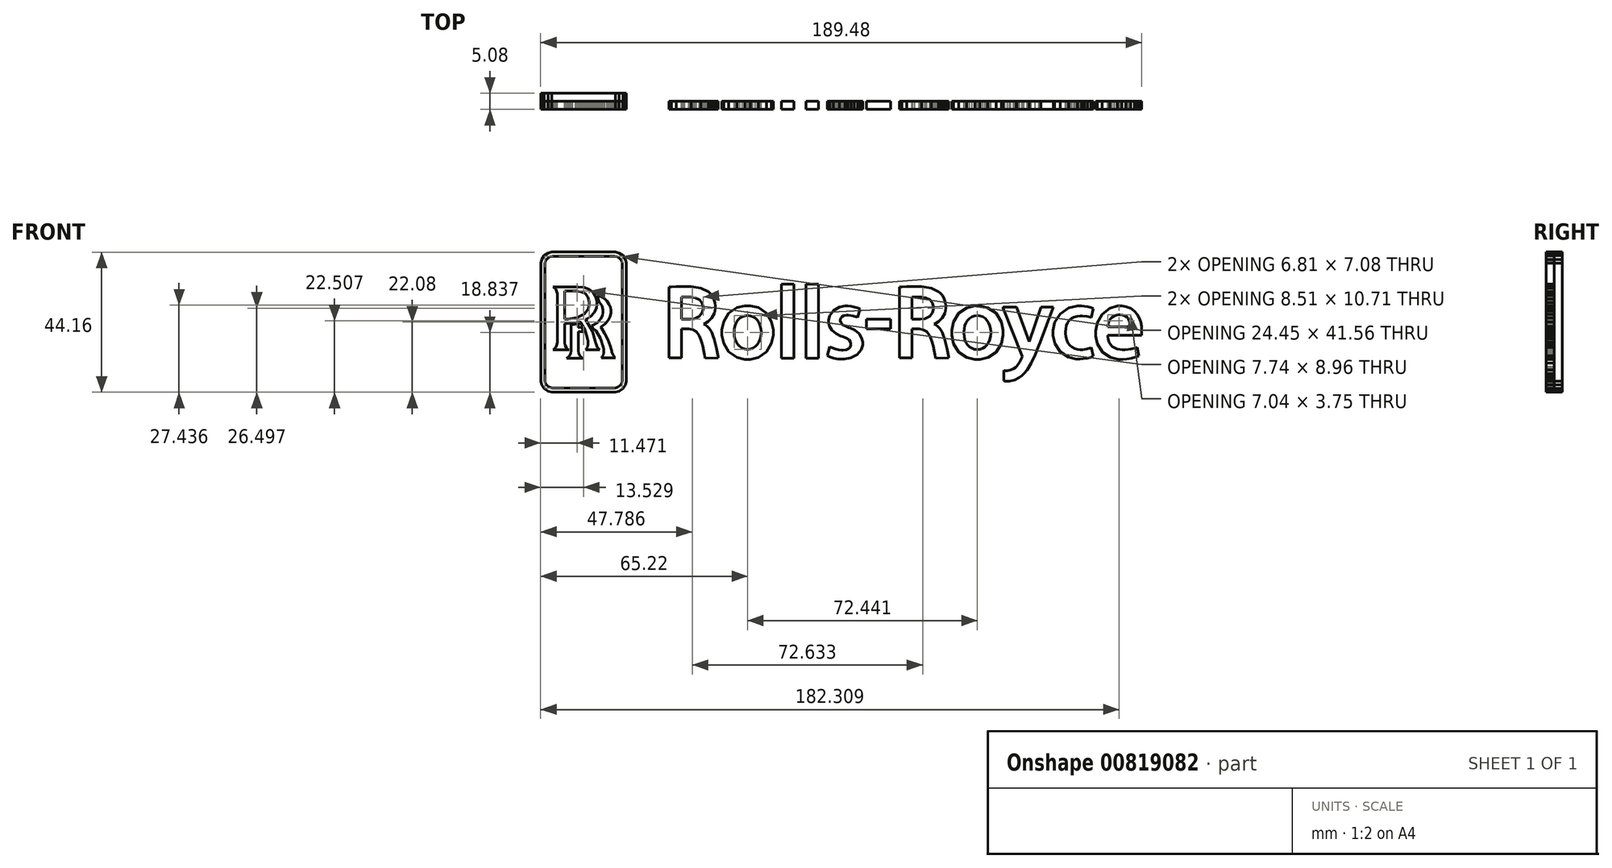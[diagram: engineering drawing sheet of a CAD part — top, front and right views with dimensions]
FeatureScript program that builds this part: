
annotation { "Feature Type Name" : "Feature", "Feature Type Description" : "" }
export const myFeature = defineFeature(function(context is Context, id is Id, definition is map)
    precondition{}
    {
        {
            var Q0;
            Q0=qCreatedBy(makeId("Front.planeOp"),FACE);
            var sketch = newSketch(context, id + "F0", { "sketchPlane" : qUnion([Q0])});
            skLineSegment(sketch, "E0", {"start": v(-93.44, 18.27) * mm, "end": v(-93.44, 18.51) * mm});
            skLineSegment(sketch, "E1", {"start": v(-93.44, 18.51) * mm, "end": v(-93.24, 19.24) * mm});
            skLineSegment(sketch, "E2", {"start": v(-93.24, 19.24) * mm, "end": v(-92.7, 20.05) * mm});
            skLineSegment(sketch, "E3", {"start": v(-92.7, 20.05) * mm, "end": v(-91.9, 20.59) * mm});
            skLineSegment(sketch, "E4", {"start": v(-91.9, 20.59) * mm, "end": v(-91.16, 20.78) * mm});
            skLineSegment(sketch, "E5", {"start": v(-91.16, 20.78) * mm, "end": v(-90.92, 20.78) * mm});
            skLineSegment(sketch, "E6", {"start": v(-90.92, 20.78) * mm, "end": v(-71.52, 20.78) * mm});
            skLineSegment(sketch, "E7", {"start": v(-71.52, 20.78) * mm, "end": v(-71.28, 20.78) * mm});
            skLineSegment(sketch, "E8", {"start": v(-71.28, 20.78) * mm, "end": v(-70.53, 20.59) * mm});
            skLineSegment(sketch, "E9", {"start": v(-70.53, 20.59) * mm, "end": v(-69.73, 20.05) * mm});
            skLineSegment(sketch, "E10", {"start": v(-69.73, 20.05) * mm, "end": v(-69.18, 19.24) * mm});
            skLineSegment(sketch, "E11", {"start": v(-69.18, 19.24) * mm, "end": v(-68.98, 18.51) * mm});
            skLineSegment(sketch, "E12", {"start": v(-68.98, 18.51) * mm, "end": v(-68.98, 18.27) * mm});
            skLineSegment(sketch, "E13", {"start": v(-68.98, 18.27) * mm, "end": v(-68.98, -18.26) * mm});
            skLineSegment(sketch, "E14", {"start": v(-68.98, -18.26) * mm, "end": v(-68.98, -18.5) * mm});
            skLineSegment(sketch, "E15", {"start": v(-68.98, -18.5) * mm, "end": v(-69.18, -19.24) * mm});
            skLineSegment(sketch, "E16", {"start": v(-69.18, -19.24) * mm, "end": v(-69.73, -20.04) * mm});
            skLineSegment(sketch, "E17", {"start": v(-69.73, -20.04) * mm, "end": v(-70.53, -20.58) * mm});
            skLineSegment(sketch, "E18", {"start": v(-70.53, -20.58) * mm, "end": v(-71.28, -20.78) * mm});
            skLineSegment(sketch, "E19", {"start": v(-71.28, -20.78) * mm, "end": v(-71.52, -20.78) * mm});
            skLineSegment(sketch, "E20", {"start": v(-71.52, -20.78) * mm, "end": v(-90.92, -20.78) * mm});
            skLineSegment(sketch, "E21", {"start": v(-90.92, -20.78) * mm, "end": v(-91.16, -20.78) * mm});
            skLineSegment(sketch, "E22", {"start": v(-91.16, -20.78) * mm, "end": v(-91.9, -20.58) * mm});
            skLineSegment(sketch, "E23", {"start": v(-91.9, -20.58) * mm, "end": v(-92.7, -20.04) * mm});
            skLineSegment(sketch, "E24", {"start": v(-92.7, -20.04) * mm, "end": v(-93.24, -19.24) * mm});
            skLineSegment(sketch, "E25", {"start": v(-93.24, -19.24) * mm, "end": v(-93.44, -18.5) * mm});
            skLineSegment(sketch, "E26", {"start": v(-93.44, -18.5) * mm, "end": v(-93.44, -18.26) * mm});
            skLineSegment(sketch, "E27", {"start": v(-93.44, -18.26) * mm, "end": v(-93.44, 18.27) * mm});
            skLineSegment(sketch, "E28", {"start": v(-18.65, -11.37) * mm, "end": v(-14.94, -11.37) * mm});
            skLineSegment(sketch, "E29", {"start": v(-14.94, -11.37) * mm, "end": v(-14.94, 12.03) * mm});
            skLineSegment(sketch, "E30", {"start": v(-14.94, 12.03) * mm, "end": v(-18.84, 12.03) * mm});
            skLineSegment(sketch, "E31", {"start": v(-18.84, 12.03) * mm, "end": v(-18.84, -11.37) * mm});
            skLineSegment(sketch, "E32", {"start": v(-18.84, -11.37) * mm, "end": v(-18.65, -11.37) * mm});
            skLineSegment(sketch, "E33", {"start": v(-10.88, -11.37) * mm, "end": v(-7.17, -11.37) * mm});
            skLineSegment(sketch, "E34", {"start": v(-7.17, -11.37) * mm, "end": v(-7.17, 12.03) * mm});
            skLineSegment(sketch, "E35", {"start": v(-7.17, 12.03) * mm, "end": v(-11.07, 12.03) * mm});
            skLineSegment(sketch, "E36", {"start": v(-11.07, 12.03) * mm, "end": v(-11.07, -11.37) * mm});
            skLineSegment(sketch, "E37", {"start": v(-11.07, -11.37) * mm, "end": v(-10.88, -11.37) * mm});
            skLineSegment(sketch, "E38", {"start": v(51.25, -18.5) * mm, "end": v(51.68, -18.57) * mm});
            skLineSegment(sketch, "E39", {"start": v(51.68, -18.57) * mm, "end": v(53, -18.56) * mm});
            skLineSegment(sketch, "E40", {"start": v(53, -18.56) * mm, "end": v(54.62, -18.2) * mm});
            skLineSegment(sketch, "E41", {"start": v(54.62, -18.2) * mm, "end": v(56.05, -17.5) * mm});
            skLineSegment(sketch, "E42", {"start": v(56.05, -17.5) * mm, "end": v(56.97, -16.84) * mm});
            skLineSegment(sketch, "E43", {"start": v(56.97, -16.84) * mm, "end": v(57.25, -16.58) * mm});
            skLineSegment(sketch, "E44", {"start": v(57.25, -16.58) * mm, "end": v(57.63, -16.22) * mm});
            skLineSegment(sketch, "E45", {"start": v(57.63, -16.22) * mm, "end": v(58.64, -15) * mm});
            skLineSegment(sketch, "E46", {"start": v(58.64, -15) * mm, "end": v(59.9, -12.96) * mm});
            skLineSegment(sketch, "E47", {"start": v(59.9, -12.96) * mm, "end": v(61.2, -10.18) * mm});
            skLineSegment(sketch, "E48", {"start": v(61.2, -10.18) * mm, "end": v(62.32, -7.37) * mm});
            skLineSegment(sketch, "E49", {"start": v(62.32, -7.37) * mm, "end": v(62.67, -6.42) * mm});
            skLineSegment(sketch, "E50", {"start": v(62.67, -6.42) * mm, "end": v(66.77, 4.5) * mm});
            skLineSegment(sketch, "E51", {"start": v(66.77, 4.5) * mm, "end": v(66.85, 4.74) * mm});
            skLineSegment(sketch, "E52", {"start": v(66.85, 4.74) * mm, "end": v(62.92, 4.74) * mm});
            skLineSegment(sketch, "E53", {"start": v(62.92, 4.74) * mm, "end": v(62.88, 4.63) * mm});
            skLineSegment(sketch, "E54", {"start": v(62.88, 4.63) * mm, "end": v(59.2, -6.21) * mm});
            skLineSegment(sketch, "E55", {"start": v(59.2, -6.21) * mm, "end": v(55.26, 4.63) * mm});
            skLineSegment(sketch, "E56", {"start": v(55.26, 4.63) * mm, "end": v(55.22, 4.74) * mm});
            skLineSegment(sketch, "E57", {"start": v(55.22, 4.74) * mm, "end": v(50.93, 4.74) * mm});
            skLineSegment(sketch, "E58", {"start": v(50.93, 4.74) * mm, "end": v(51.02, 4.5) * mm});
            skLineSegment(sketch, "E59", {"start": v(51.02, 4.5) * mm, "end": v(57.14, -10.84) * mm});
            skLineSegment(sketch, "E60", {"start": v(57.14, -10.84) * mm, "end": v(57.02, -11.18) * mm});
            skLineSegment(sketch, "E61", {"start": v(57.02, -11.18) * mm, "end": v(56.22, -12.7) * mm});
            skLineSegment(sketch, "E62", {"start": v(56.22, -12.7) * mm, "end": v(55.29, -13.93) * mm});
            skLineSegment(sketch, "E63", {"start": v(55.29, -13.93) * mm, "end": v(55.1, -14.13) * mm});
            skLineSegment(sketch, "E64", {"start": v(55.1, -14.13) * mm, "end": v(54.91, -14.3) * mm});
            skLineSegment(sketch, "E65", {"start": v(54.91, -14.3) * mm, "end": v(54.29, -14.73) * mm});
            skLineSegment(sketch, "E66", {"start": v(54.29, -14.73) * mm, "end": v(53.36, -15.13) * mm});
            skLineSegment(sketch, "E67", {"start": v(53.36, -15.13) * mm, "end": v(52.34, -15.3) * mm});
            skLineSegment(sketch, "E68", {"start": v(52.34, -15.3) * mm, "end": v(51.52, -15.28) * mm});
            skLineSegment(sketch, "E69", {"start": v(51.52, -15.28) * mm, "end": v(51.25, -15.24) * mm});
            skLineSegment(sketch, "E70", {"start": v(51.25, -15.24) * mm, "end": v(51.25, -18.5) * mm});
            skLineSegment(sketch, "E71", {"start": v(42.93, 5.14) * mm, "end": v(42.1, 5.14) * mm});
            skLineSegment(sketch, "E72", {"start": v(42.1, 5.14) * mm, "end": v(39.63, 4.52) * mm});
            skLineSegment(sketch, "E73", {"start": v(39.63, 4.52) * mm, "end": v(37.06, 2.78) * mm});
            skLineSegment(sketch, "E74", {"start": v(37.06, 2.78) * mm, "end": v(35.4, 0.11) * mm});
            skLineSegment(sketch, "E75", {"start": v(35.4, 0.11) * mm, "end": v(34.8, -2.45) * mm});
            skLineSegment(sketch, "E76", {"start": v(34.8, -2.45) * mm, "end": v(34.8, -3.3) * mm});
            skLineSegment(sketch, "E77", {"start": v(34.8, -3.3) * mm, "end": v(34.8, -4.17) * mm});
            skLineSegment(sketch, "E78", {"start": v(34.8, -4.17) * mm, "end": v(35.39, -6.76) * mm});
            skLineSegment(sketch, "E79", {"start": v(35.39, -6.76) * mm, "end": v(37.04, -9.44) * mm});
            skLineSegment(sketch, "E80", {"start": v(37.04, -9.44) * mm, "end": v(39.6, -11.16) * mm});
            skLineSegment(sketch, "E81", {"start": v(39.6, -11.16) * mm, "end": v(42.1, -11.78) * mm});
            skLineSegment(sketch, "E82", {"start": v(42.1, -11.78) * mm, "end": v(42.93, -11.78) * mm});
            skLineSegment(sketch, "E83", {"start": v(42.93, -11.78) * mm, "end": v(43.76, -11.78) * mm});
            skLineSegment(sketch, "E84", {"start": v(43.76, -11.78) * mm, "end": v(46.25, -11.16) * mm});
            skLineSegment(sketch, "E85", {"start": v(46.25, -11.16) * mm, "end": v(48.8, -9.44) * mm});
            skLineSegment(sketch, "E86", {"start": v(48.8, -9.44) * mm, "end": v(50.46, -6.76) * mm});
            skLineSegment(sketch, "E87", {"start": v(50.46, -6.76) * mm, "end": v(51.04, -4.17) * mm});
            skLineSegment(sketch, "E88", {"start": v(51.04, -4.17) * mm, "end": v(51.04, -3.3) * mm});
            skLineSegment(sketch, "E89", {"start": v(51.04, -3.3) * mm, "end": v(51.04, -2.45) * mm});
            skLineSegment(sketch, "E90", {"start": v(51.04, -2.45) * mm, "end": v(50.45, 0.11) * mm});
            skLineSegment(sketch, "E91", {"start": v(50.45, 0.11) * mm, "end": v(48.78, 2.78) * mm});
            skLineSegment(sketch, "E92", {"start": v(48.78, 2.78) * mm, "end": v(46.22, 4.52) * mm});
            skLineSegment(sketch, "E93", {"start": v(46.22, 4.52) * mm, "end": v(43.75, 5.14) * mm});
            skLineSegment(sketch, "E94", {"start": v(43.75, 5.14) * mm, "end": v(42.93, 5.14) * mm});
            skLineSegment(sketch, "E95", {"start": v(42.9, -8.64) * mm, "end": v(42.69, -8.64) * mm});
            skLineSegment(sketch, "E96", {"start": v(42.69, -8.64) * mm, "end": v(42.03, -8.54) * mm});
            skLineSegment(sketch, "E97", {"start": v(42.03, -8.54) * mm, "end": v(41.22, -8.26) * mm});
            skLineSegment(sketch, "E98", {"start": v(41.22, -8.26) * mm, "end": v(40.5, -7.8) * mm});
            skLineSegment(sketch, "E99", {"start": v(40.5, -7.8) * mm, "end": v(39.87, -7.18) * mm});
            skLineSegment(sketch, "E100", {"start": v(39.87, -7.18) * mm, "end": v(39.36, -6.4) * mm});
            skLineSegment(sketch, "E101", {"start": v(39.36, -6.4) * mm, "end": v(38.98, -5.5) * mm});
            skLineSegment(sketch, "E102", {"start": v(38.98, -5.5) * mm, "end": v(38.75, -4.45) * mm});
            skLineSegment(sketch, "E103", {"start": v(38.75, -4.45) * mm, "end": v(38.66, -3.58) * mm});
            skLineSegment(sketch, "E104", {"start": v(38.66, -3.58) * mm, "end": v(38.66, -3.29) * mm});
            skLineSegment(sketch, "E105", {"start": v(38.66, -3.29) * mm, "end": v(38.66, -3) * mm});
            skLineSegment(sketch, "E106", {"start": v(38.66, -3) * mm, "end": v(38.75, -2.12) * mm});
            skLineSegment(sketch, "E107", {"start": v(38.75, -2.12) * mm, "end": v(38.98, -1.08) * mm});
            skLineSegment(sketch, "E108", {"start": v(38.98, -1.08) * mm, "end": v(39.36, -0.17) * mm});
            skLineSegment(sketch, "E109", {"start": v(39.36, -0.17) * mm, "end": v(39.87, 0.6) * mm});
            skLineSegment(sketch, "E110", {"start": v(39.87, 0.6) * mm, "end": v(40.5, 1.23) * mm});
            skLineSegment(sketch, "E111", {"start": v(40.5, 1.23) * mm, "end": v(41.22, 1.7) * mm});
            skLineSegment(sketch, "E112", {"start": v(41.22, 1.7) * mm, "end": v(42.03, 1.97) * mm});
            skLineSegment(sketch, "E113", {"start": v(42.03, 1.97) * mm, "end": v(42.69, 2.07) * mm});
            skLineSegment(sketch, "E114", {"start": v(42.69, 2.07) * mm, "end": v(42.9, 2.07) * mm});
            skLineSegment(sketch, "E115", {"start": v(42.9, 2.07) * mm, "end": v(43.13, 2.07) * mm});
            skLineSegment(sketch, "E116", {"start": v(43.13, 2.07) * mm, "end": v(43.8, 1.97) * mm});
            skLineSegment(sketch, "E117", {"start": v(43.8, 1.97) * mm, "end": v(44.62, 1.7) * mm});
            skLineSegment(sketch, "E118", {"start": v(44.62, 1.7) * mm, "end": v(45.35, 1.23) * mm});
            skLineSegment(sketch, "E119", {"start": v(45.35, 1.23) * mm, "end": v(45.97, 0.6) * mm});
            skLineSegment(sketch, "E120", {"start": v(45.97, 0.6) * mm, "end": v(46.48, -0.17) * mm});
            skLineSegment(sketch, "E121", {"start": v(46.48, -0.17) * mm, "end": v(46.86, -1.08) * mm});
            skLineSegment(sketch, "E122", {"start": v(46.86, -1.08) * mm, "end": v(47.1, -2.12) * mm});
            skLineSegment(sketch, "E123", {"start": v(47.1, -2.12) * mm, "end": v(47.18, -3) * mm});
            skLineSegment(sketch, "E124", {"start": v(47.18, -3) * mm, "end": v(47.18, -3.29) * mm});
            skLineSegment(sketch, "E125", {"start": v(47.18, -3.29) * mm, "end": v(47.18, -3.58) * mm});
            skLineSegment(sketch, "E126", {"start": v(47.18, -3.58) * mm, "end": v(47.1, -4.45) * mm});
            skLineSegment(sketch, "E127", {"start": v(47.1, -4.45) * mm, "end": v(46.86, -5.5) * mm});
            skLineSegment(sketch, "E128", {"start": v(46.86, -5.5) * mm, "end": v(46.47, -6.4) * mm});
            skLineSegment(sketch, "E129", {"start": v(46.47, -6.4) * mm, "end": v(45.96, -7.18) * mm});
            skLineSegment(sketch, "E130", {"start": v(45.96, -7.18) * mm, "end": v(45.34, -7.8) * mm});
            skLineSegment(sketch, "E131", {"start": v(45.34, -7.8) * mm, "end": v(44.61, -8.26) * mm});
            skLineSegment(sketch, "E132", {"start": v(44.61, -8.26) * mm, "end": v(43.8, -8.54) * mm});
            skLineSegment(sketch, "E133", {"start": v(43.8, -8.54) * mm, "end": v(43.13, -8.64) * mm});
            skLineSegment(sketch, "E134", {"start": v(43.13, -8.64) * mm, "end": v(42.9, -8.64) * mm});
            skLineSegment(sketch, "E135", {"start": v(-29.51, 5.18) * mm, "end": v(-30.35, 5.18) * mm});
            skLineSegment(sketch, "E136", {"start": v(-30.35, 5.18) * mm, "end": v(-32.87, 4.57) * mm});
            skLineSegment(sketch, "E137", {"start": v(-32.87, 4.57) * mm, "end": v(-35.43, 2.85) * mm});
            skLineSegment(sketch, "E138", {"start": v(-35.43, 2.85) * mm, "end": v(-37.07, 0.18) * mm});
            skLineSegment(sketch, "E139", {"start": v(-37.07, 0.18) * mm, "end": v(-37.64, -2.4) * mm});
            skLineSegment(sketch, "E140", {"start": v(-37.64, -2.4) * mm, "end": v(-37.64, -3.26) * mm});
            skLineSegment(sketch, "E141", {"start": v(-37.64, -3.26) * mm, "end": v(-37.64, -4.13) * mm});
            skLineSegment(sketch, "E142", {"start": v(-37.64, -4.13) * mm, "end": v(-37.07, -6.72) * mm});
            skLineSegment(sketch, "E143", {"start": v(-37.07, -6.72) * mm, "end": v(-35.43, -9.4) * mm});
            skLineSegment(sketch, "E144", {"start": v(-35.43, -9.4) * mm, "end": v(-32.87, -11.12) * mm});
            skLineSegment(sketch, "E145", {"start": v(-32.87, -11.12) * mm, "end": v(-30.35, -11.74) * mm});
            skLineSegment(sketch, "E146", {"start": v(-30.35, -11.74) * mm, "end": v(-29.51, -11.74) * mm});
            skLineSegment(sketch, "E147", {"start": v(-29.51, -11.74) * mm, "end": v(-28.67, -11.74) * mm});
            skLineSegment(sketch, "E148", {"start": v(-28.67, -11.74) * mm, "end": v(-26.15, -11.12) * mm});
            skLineSegment(sketch, "E149", {"start": v(-26.15, -11.12) * mm, "end": v(-23.6, -9.4) * mm});
            skLineSegment(sketch, "E150", {"start": v(-23.6, -9.4) * mm, "end": v(-21.97, -6.72) * mm});
            skLineSegment(sketch, "E151", {"start": v(-21.97, -6.72) * mm, "end": v(-21.4, -4.13) * mm});
            skLineSegment(sketch, "E152", {"start": v(-21.4, -4.13) * mm, "end": v(-21.4, -3.26) * mm});
            skLineSegment(sketch, "E153", {"start": v(-21.4, -3.26) * mm, "end": v(-21.4, -2.4) * mm});
            skLineSegment(sketch, "E154", {"start": v(-21.4, -2.4) * mm, "end": v(-21.97, 0.18) * mm});
            skLineSegment(sketch, "E155", {"start": v(-21.97, 0.18) * mm, "end": v(-23.6, 2.85) * mm});
            skLineSegment(sketch, "E156", {"start": v(-23.6, 2.85) * mm, "end": v(-26.15, 4.57) * mm});
            skLineSegment(sketch, "E157", {"start": v(-26.15, 4.57) * mm, "end": v(-28.67, 5.18) * mm});
            skLineSegment(sketch, "E158", {"start": v(-28.67, 5.18) * mm, "end": v(-29.51, 5.18) * mm});
            skLineSegment(sketch, "E159", {"start": v(-29.53, -8.6) * mm, "end": v(-29.75, -8.6) * mm});
            skLineSegment(sketch, "E160", {"start": v(-29.75, -8.6) * mm, "end": v(-30.41, -8.5) * mm});
            skLineSegment(sketch, "E161", {"start": v(-30.41, -8.5) * mm, "end": v(-31.22, -8.21) * mm});
            skLineSegment(sketch, "E162", {"start": v(-31.22, -8.21) * mm, "end": v(-31.94, -7.75) * mm});
            skLineSegment(sketch, "E163", {"start": v(-31.94, -7.75) * mm, "end": v(-32.57, -7.13) * mm});
            skLineSegment(sketch, "E164", {"start": v(-32.57, -7.13) * mm, "end": v(-33.07, -6.35) * mm});
            skLineSegment(sketch, "E165", {"start": v(-33.07, -6.35) * mm, "end": v(-33.46, -5.44) * mm});
            skLineSegment(sketch, "E166", {"start": v(-33.46, -5.44) * mm, "end": v(-33.7, -4.4) * mm});
            skLineSegment(sketch, "E167", {"start": v(-33.7, -4.4) * mm, "end": v(-33.78, -3.53) * mm});
            skLineSegment(sketch, "E168", {"start": v(-33.78, -3.53) * mm, "end": v(-33.78, -3.24) * mm});
            skLineSegment(sketch, "E169", {"start": v(-33.78, -3.24) * mm, "end": v(-33.78, -2.95) * mm});
            skLineSegment(sketch, "E170", {"start": v(-33.78, -2.95) * mm, "end": v(-33.7, -2.08) * mm});
            skLineSegment(sketch, "E171", {"start": v(-33.7, -2.08) * mm, "end": v(-33.46, -1.04) * mm});
            skLineSegment(sketch, "E172", {"start": v(-33.46, -1.04) * mm, "end": v(-33.07, -0.12) * mm});
            skLineSegment(sketch, "E173", {"start": v(-33.07, -0.12) * mm, "end": v(-32.57, 0.65) * mm});
            skLineSegment(sketch, "E174", {"start": v(-32.57, 0.65) * mm, "end": v(-31.94, 1.27) * mm});
            skLineSegment(sketch, "E175", {"start": v(-31.94, 1.27) * mm, "end": v(-31.22, 1.73) * mm});
            skLineSegment(sketch, "E176", {"start": v(-31.22, 1.73) * mm, "end": v(-30.41, 2.02) * mm});
            skLineSegment(sketch, "E177", {"start": v(-30.41, 2.02) * mm, "end": v(-29.75, 2.11) * mm});
            skLineSegment(sketch, "E178", {"start": v(-29.75, 2.11) * mm, "end": v(-29.53, 2.11) * mm});
            skLineSegment(sketch, "E179", {"start": v(-29.53, 2.11) * mm, "end": v(-29.3, 2.11) * mm});
            skLineSegment(sketch, "E180", {"start": v(-29.3, 2.11) * mm, "end": v(-28.64, 2.02) * mm});
            skLineSegment(sketch, "E181", {"start": v(-28.64, 2.02) * mm, "end": v(-27.82, 1.73) * mm});
            skLineSegment(sketch, "E182", {"start": v(-27.82, 1.73) * mm, "end": v(-27.1, 1.27) * mm});
            skLineSegment(sketch, "E183", {"start": v(-27.1, 1.27) * mm, "end": v(-26.47, 0.65) * mm});
            skLineSegment(sketch, "E184", {"start": v(-26.47, 0.65) * mm, "end": v(-25.96, -0.12) * mm});
            skLineSegment(sketch, "E185", {"start": v(-25.96, -0.12) * mm, "end": v(-25.58, -1.04) * mm});
            skLineSegment(sketch, "E186", {"start": v(-25.58, -1.04) * mm, "end": v(-25.35, -2.08) * mm});
            skLineSegment(sketch, "E187", {"start": v(-25.35, -2.08) * mm, "end": v(-25.26, -2.95) * mm});
            skLineSegment(sketch, "E188", {"start": v(-25.26, -2.95) * mm, "end": v(-25.26, -3.24) * mm});
            skLineSegment(sketch, "E189", {"start": v(-25.26, -3.24) * mm, "end": v(-25.26, -3.53) * mm});
            skLineSegment(sketch, "E190", {"start": v(-25.26, -3.53) * mm, "end": v(-25.35, -4.4) * mm});
            skLineSegment(sketch, "E191", {"start": v(-25.35, -4.4) * mm, "end": v(-25.59, -5.44) * mm});
            skLineSegment(sketch, "E192", {"start": v(-25.59, -5.44) * mm, "end": v(-25.97, -6.35) * mm});
            skLineSegment(sketch, "E193", {"start": v(-25.97, -6.35) * mm, "end": v(-26.48, -7.13) * mm});
            skLineSegment(sketch, "E194", {"start": v(-26.48, -7.13) * mm, "end": v(-27.1, -7.75) * mm});
            skLineSegment(sketch, "E195", {"start": v(-27.1, -7.75) * mm, "end": v(-27.83, -8.21) * mm});
            skLineSegment(sketch, "E196", {"start": v(-27.83, -8.21) * mm, "end": v(-28.64, -8.5) * mm});
            skLineSegment(sketch, "E197", {"start": v(-28.64, -8.5) * mm, "end": v(-29.3, -8.6) * mm});
            skLineSegment(sketch, "E198", {"start": v(-29.3, -8.6) * mm, "end": v(-29.53, -8.6) * mm});
            skLineSegment(sketch, "E199", {"start": v(7.92, -2.07) * mm, "end": v(15.58, -2.07) * mm});
            skLineSegment(sketch, "E200", {"start": v(15.58, -2.07) * mm, "end": v(15.58, 0.87) * mm});
            skLineSegment(sketch, "E201", {"start": v(15.58, 0.87) * mm, "end": v(7.92, 0.87) * mm});
            skLineSegment(sketch, "E202", {"start": v(7.92, 0.87) * mm, "end": v(7.92, -2.07) * mm});
            skLineSegment(sketch, "E203", {"start": v(-40.29, -4.65) * mm, "end": v(-40.08, -5.3) * mm});
            skLineSegment(sketch, "E204", {"start": v(-40.08, -5.3) * mm, "end": v(-39.33, -8.36) * mm});
            skLineSegment(sketch, "E205", {"start": v(-39.33, -8.36) * mm, "end": v(-38.82, -10.92) * mm});
            skLineSegment(sketch, "E206", {"start": v(-38.82, -10.92) * mm, "end": v(-38.75, -11.3) * mm});
            skLineSegment(sketch, "E207", {"start": v(-38.75, -11.3) * mm, "end": v(-42.91, -11.33) * mm});
            skLineSegment(sketch, "E208", {"start": v(-42.91, -11.33) * mm, "end": v(-42.96, -11.06) * mm});
            skLineSegment(sketch, "E209", {"start": v(-42.96, -11.06) * mm, "end": v(-43.1, -10.24) * mm});
            skLineSegment(sketch, "E210", {"start": v(-43.1, -10.24) * mm, "end": v(-43.32, -8.98) * mm});
            skLineSegment(sketch, "E211", {"start": v(-43.32, -8.98) * mm, "end": v(-43.65, -7.54) * mm});
            skLineSegment(sketch, "E212", {"start": v(-43.65, -7.54) * mm, "end": v(-43.98, -6.34) * mm});
            skLineSegment(sketch, "E213", {"start": v(-43.98, -6.34) * mm, "end": v(-44.1, -5.95) * mm});
            skLineSegment(sketch, "E214", {"start": v(-44.1, -5.95) * mm, "end": v(-44.24, -5.51) * mm});
            skLineSegment(sketch, "E215", {"start": v(-44.24, -5.51) * mm, "end": v(-44.79, -4.23) * mm});
            skLineSegment(sketch, "E216", {"start": v(-44.79, -4.23) * mm, "end": v(-45.67, -3.03) * mm});
            skLineSegment(sketch, "E217", {"start": v(-45.67, -3.03) * mm, "end": v(-46.85, -2.32) * mm});
            skLineSegment(sketch, "E218", {"start": v(-46.85, -2.32) * mm, "end": v(-48.06, -2.1) * mm});
            skLineSegment(sketch, "E219", {"start": v(-48.06, -2.1) * mm, "end": v(-48.46, -2.1) * mm});
            skLineSegment(sketch, "E220", {"start": v(-48.46, -2.1) * mm, "end": v(-50.36, -2.1) * mm});
            skLineSegment(sketch, "E221", {"start": v(-50.36, -2.1) * mm, "end": v(-50.36, -11.3) * mm});
            skLineSegment(sketch, "E222", {"start": v(-50.36, -11.3) * mm, "end": v(-54.28, -11.3) * mm});
            skLineSegment(sketch, "E223", {"start": v(-54.28, -11.3) * mm, "end": v(-54.28, 11.12) * mm});
            skLineSegment(sketch, "E224", {"start": v(-54.28, 11.12) * mm, "end": v(-53.57, 11.12) * mm});
            skLineSegment(sketch, "E225", {"start": v(-53.57, 11.12) * mm, "end": v(-51.96, 11.18) * mm});
            skLineSegment(sketch, "E226", {"start": v(-51.96, 11.18) * mm, "end": v(-51.42, 11.18) * mm});
            skLineSegment(sketch, "E227", {"start": v(-51.42, 11.18) * mm, "end": v(-48.27, 11.18) * mm});
            skLineSegment(sketch, "E228", {"start": v(-48.27, 11.18) * mm, "end": v(-47.26, 11.18) * mm});
            skLineSegment(sketch, "E229", {"start": v(-47.26, 11.18) * mm, "end": v(-44.26, 10.7) * mm});
            skLineSegment(sketch, "E230", {"start": v(-44.26, 10.7) * mm, "end": v(-41.9, 9.58) * mm});
            skLineSegment(sketch, "E231", {"start": v(-41.9, 9.58) * mm, "end": v(-41.54, 9.26) * mm});
            skLineSegment(sketch, "E232", {"start": v(-41.54, 9.26) * mm, "end": v(-41.32, 9.07) * mm});
            skLineSegment(sketch, "E233", {"start": v(-41.32, 9.07) * mm, "end": v(-40.74, 8.38) * mm});
            skLineSegment(sketch, "E234", {"start": v(-40.74, 8.38) * mm, "end": v(-40.15, 7.33) * mm});
            skLineSegment(sketch, "E235", {"start": v(-40.15, 7.33) * mm, "end": v(-39.79, 6.13) * mm});
            skLineSegment(sketch, "E236", {"start": v(-39.79, 6.13) * mm, "end": v(-39.67, 5.15) * mm});
            skLineSegment(sketch, "E237", {"start": v(-39.67, 5.15) * mm, "end": v(-39.67, 4.82) * mm});
            skLineSegment(sketch, "E238", {"start": v(-39.67, 4.82) * mm, "end": v(-39.67, 4.33) * mm});
            skLineSegment(sketch, "E239", {"start": v(-39.67, 4.33) * mm, "end": v(-39.97, 2.83) * mm});
            skLineSegment(sketch, "E240", {"start": v(-39.97, 2.83) * mm, "end": v(-40.77, 1.28) * mm});
            skLineSegment(sketch, "E241", {"start": v(-40.77, 1.28) * mm, "end": v(-41.94, 0.15) * mm});
            skLineSegment(sketch, "E242", {"start": v(-41.94, 0.15) * mm, "end": v(-42.95, -0.46) * mm});
            skLineSegment(sketch, "E243", {"start": v(-42.95, -0.46) * mm, "end": v(-43.32, -0.6) * mm});
            skLineSegment(sketch, "E244", {"start": v(-43.32, -0.6) * mm, "end": v(-43.06, -0.72) * mm});
            skLineSegment(sketch, "E245", {"start": v(-43.06, -0.72) * mm, "end": v(-42.35, -1.2) * mm});
            skLineSegment(sketch, "E246", {"start": v(-42.35, -1.2) * mm, "end": v(-41.54, -2.03) * mm});
            skLineSegment(sketch, "E247", {"start": v(-41.54, -2.03) * mm, "end": v(-40.87, -3.17) * mm});
            skLineSegment(sketch, "E248", {"start": v(-40.87, -3.17) * mm, "end": v(-40.4, -4.27) * mm});
            skLineSegment(sketch, "E249", {"start": v(-40.4, -4.27) * mm, "end": v(-40.29, -4.65) * mm});
            skLineSegment(sketch, "E250", {"start": v(-47.86, 7.96) * mm, "end": v(-49.16, 7.96) * mm});
            skLineSegment(sketch, "E251", {"start": v(-49.16, 7.96) * mm, "end": v(-49.34, 7.96) * mm});
            skLineSegment(sketch, "E252", {"start": v(-49.34, 7.96) * mm, "end": v(-49.86, 7.94) * mm});
            skLineSegment(sketch, "E253", {"start": v(-49.86, 7.94) * mm, "end": v(-50.23, 7.92) * mm});
            skLineSegment(sketch, "E254", {"start": v(-50.23, 7.92) * mm, "end": v(-50.36, 7.92) * mm});
            skLineSegment(sketch, "E255", {"start": v(-50.36, 7.92) * mm, "end": v(-50.36, 0.88) * mm});
            skLineSegment(sketch, "E256", {"start": v(-50.36, 0.88) * mm, "end": v(-48.08, 0.88) * mm});
            skLineSegment(sketch, "E257", {"start": v(-48.08, 0.88) * mm, "end": v(-47.61, 0.88) * mm});
            skLineSegment(sketch, "E258", {"start": v(-47.61, 0.88) * mm, "end": v(-46.23, 1.13) * mm});
            skLineSegment(sketch, "E259", {"start": v(-46.23, 1.13) * mm, "end": v(-44.8, 1.84) * mm});
            skLineSegment(sketch, "E260", {"start": v(-44.8, 1.84) * mm, "end": v(-43.88, 2.97) * mm});
            skLineSegment(sketch, "E261", {"start": v(-43.88, 2.97) * mm, "end": v(-43.55, 4.09) * mm});
            skLineSegment(sketch, "E262", {"start": v(-43.55, 4.09) * mm, "end": v(-43.55, 4.46) * mm});
            skLineSegment(sketch, "E263", {"start": v(-43.55, 4.46) * mm, "end": v(-43.55, 4.84) * mm});
            skLineSegment(sketch, "E264", {"start": v(-43.55, 4.84) * mm, "end": v(-43.83, 5.97) * mm});
            skLineSegment(sketch, "E265", {"start": v(-43.83, 5.97) * mm, "end": v(-44.65, 7.06) * mm});
            skLineSegment(sketch, "E266", {"start": v(-44.65, 7.06) * mm, "end": v(-46, 7.73) * mm});
            skLineSegment(sketch, "E267", {"start": v(-46, 7.73) * mm, "end": v(-47.4, 7.96) * mm});
            skLineSegment(sketch, "E268", {"start": v(-47.4, 7.96) * mm, "end": v(-47.86, 7.96) * mm});
            skLineSegment(sketch, "E269", {"start": v(32.35, -4.65) * mm, "end": v(32.55, -5.3) * mm});
            skLineSegment(sketch, "E270", {"start": v(32.55, -5.3) * mm, "end": v(33.3, -8.36) * mm});
            skLineSegment(sketch, "E271", {"start": v(33.3, -8.36) * mm, "end": v(33.8, -10.92) * mm});
            skLineSegment(sketch, "E272", {"start": v(33.8, -10.92) * mm, "end": v(33.88, -11.3) * mm});
            skLineSegment(sketch, "E273", {"start": v(33.88, -11.3) * mm, "end": v(29.72, -11.33) * mm});
            skLineSegment(sketch, "E274", {"start": v(29.72, -11.33) * mm, "end": v(29.68, -11.06) * mm});
            skLineSegment(sketch, "E275", {"start": v(29.68, -11.06) * mm, "end": v(29.54, -10.24) * mm});
            skLineSegment(sketch, "E276", {"start": v(29.54, -10.24) * mm, "end": v(29.3, -8.98) * mm});
            skLineSegment(sketch, "E277", {"start": v(29.3, -8.98) * mm, "end": v(28.99, -7.54) * mm});
            skLineSegment(sketch, "E278", {"start": v(28.99, -7.54) * mm, "end": v(28.66, -6.34) * mm});
            skLineSegment(sketch, "E279", {"start": v(28.66, -6.34) * mm, "end": v(28.53, -5.95) * mm});
            skLineSegment(sketch, "E280", {"start": v(28.53, -5.95) * mm, "end": v(28.39, -5.51) * mm});
            skLineSegment(sketch, "E281", {"start": v(28.39, -5.51) * mm, "end": v(27.85, -4.23) * mm});
            skLineSegment(sketch, "E282", {"start": v(27.85, -4.23) * mm, "end": v(26.97, -3.03) * mm});
            skLineSegment(sketch, "E283", {"start": v(26.97, -3.03) * mm, "end": v(25.78, -2.32) * mm});
            skLineSegment(sketch, "E284", {"start": v(25.78, -2.32) * mm, "end": v(24.58, -2.1) * mm});
            skLineSegment(sketch, "E285", {"start": v(24.58, -2.1) * mm, "end": v(24.18, -2.1) * mm});
            skLineSegment(sketch, "E286", {"start": v(24.18, -2.1) * mm, "end": v(22.28, -2.1) * mm});
            skLineSegment(sketch, "E287", {"start": v(22.28, -2.1) * mm, "end": v(22.28, -11.3) * mm});
            skLineSegment(sketch, "E288", {"start": v(22.28, -11.3) * mm, "end": v(18.35, -11.3) * mm});
            skLineSegment(sketch, "E289", {"start": v(18.35, -11.3) * mm, "end": v(18.35, 11.12) * mm});
            skLineSegment(sketch, "E290", {"start": v(18.35, 11.12) * mm, "end": v(19.06, 11.12) * mm});
            skLineSegment(sketch, "E291", {"start": v(19.06, 11.12) * mm, "end": v(20.67, 11.18) * mm});
            skLineSegment(sketch, "E292", {"start": v(20.67, 11.18) * mm, "end": v(21.2, 11.18) * mm});
            skLineSegment(sketch, "E293", {"start": v(21.2, 11.18) * mm, "end": v(24.37, 11.18) * mm});
            skLineSegment(sketch, "E294", {"start": v(24.37, 11.18) * mm, "end": v(25.37, 11.18) * mm});
            skLineSegment(sketch, "E295", {"start": v(25.37, 11.18) * mm, "end": v(28.38, 10.7) * mm});
            skLineSegment(sketch, "E296", {"start": v(28.38, 10.7) * mm, "end": v(30.73, 9.58) * mm});
            skLineSegment(sketch, "E297", {"start": v(30.73, 9.58) * mm, "end": v(31.09, 9.26) * mm});
            skLineSegment(sketch, "E298", {"start": v(31.09, 9.26) * mm, "end": v(31.31, 9.07) * mm});
            skLineSegment(sketch, "E299", {"start": v(31.31, 9.07) * mm, "end": v(31.9, 8.38) * mm});
            skLineSegment(sketch, "E300", {"start": v(31.9, 8.38) * mm, "end": v(32.48, 7.33) * mm});
            skLineSegment(sketch, "E301", {"start": v(32.48, 7.33) * mm, "end": v(32.84, 6.13) * mm});
            skLineSegment(sketch, "E302", {"start": v(32.84, 6.13) * mm, "end": v(32.97, 5.15) * mm});
            skLineSegment(sketch, "E303", {"start": v(32.97, 5.15) * mm, "end": v(32.97, 4.82) * mm});
            skLineSegment(sketch, "E304", {"start": v(32.97, 4.82) * mm, "end": v(32.97, 4.33) * mm});
            skLineSegment(sketch, "E305", {"start": v(32.97, 4.33) * mm, "end": v(32.67, 2.83) * mm});
            skLineSegment(sketch, "E306", {"start": v(32.67, 2.83) * mm, "end": v(31.86, 1.28) * mm});
            skLineSegment(sketch, "E307", {"start": v(31.86, 1.28) * mm, "end": v(30.7, 0.15) * mm});
            skLineSegment(sketch, "E308", {"start": v(30.7, 0.15) * mm, "end": v(29.68, -0.46) * mm});
            skLineSegment(sketch, "E309", {"start": v(29.68, -0.46) * mm, "end": v(29.32, -0.6) * mm});
            skLineSegment(sketch, "E310", {"start": v(29.32, -0.6) * mm, "end": v(29.57, -0.72) * mm});
            skLineSegment(sketch, "E311", {"start": v(29.57, -0.72) * mm, "end": v(30.28, -1.2) * mm});
            skLineSegment(sketch, "E312", {"start": v(30.28, -1.2) * mm, "end": v(31.09, -2.03) * mm});
            skLineSegment(sketch, "E313", {"start": v(31.09, -2.03) * mm, "end": v(31.76, -3.17) * mm});
            skLineSegment(sketch, "E314", {"start": v(31.76, -3.17) * mm, "end": v(32.22, -4.27) * mm});
            skLineSegment(sketch, "E315", {"start": v(32.22, -4.27) * mm, "end": v(32.35, -4.65) * mm});
            skLineSegment(sketch, "E316", {"start": v(24.77, 7.96) * mm, "end": v(23.47, 7.96) * mm});
            skLineSegment(sketch, "E317", {"start": v(23.47, 7.96) * mm, "end": v(23.17, 7.96) * mm});
            skLineSegment(sketch, "E318", {"start": v(23.17, 7.96) * mm, "end": v(22.5, 7.92) * mm});
            skLineSegment(sketch, "E319", {"start": v(22.5, 7.92) * mm, "end": v(22.28, 7.92) * mm});
            skLineSegment(sketch, "E320", {"start": v(22.28, 7.92) * mm, "end": v(22.28, 0.88) * mm});
            skLineSegment(sketch, "E321", {"start": v(22.28, 0.88) * mm, "end": v(24.56, 0.88) * mm});
            skLineSegment(sketch, "E322", {"start": v(24.56, 0.88) * mm, "end": v(25.02, 0.88) * mm});
            skLineSegment(sketch, "E323", {"start": v(25.02, 0.88) * mm, "end": v(26.4, 1.13) * mm});
            skLineSegment(sketch, "E324", {"start": v(26.4, 1.13) * mm, "end": v(27.83, 1.84) * mm});
            skLineSegment(sketch, "E325", {"start": v(27.83, 1.84) * mm, "end": v(28.75, 2.97) * mm});
            skLineSegment(sketch, "E326", {"start": v(28.75, 2.97) * mm, "end": v(29.08, 4.09) * mm});
            skLineSegment(sketch, "E327", {"start": v(29.08, 4.09) * mm, "end": v(29.08, 4.46) * mm});
            skLineSegment(sketch, "E328", {"start": v(29.08, 4.46) * mm, "end": v(29.08, 4.84) * mm});
            skLineSegment(sketch, "E329", {"start": v(29.08, 4.84) * mm, "end": v(28.8, 5.97) * mm});
            skLineSegment(sketch, "E330", {"start": v(28.8, 5.97) * mm, "end": v(27.98, 7.06) * mm});
            skLineSegment(sketch, "E331", {"start": v(27.98, 7.06) * mm, "end": v(26.63, 7.73) * mm});
            skLineSegment(sketch, "E332", {"start": v(26.63, 7.73) * mm, "end": v(25.24, 7.96) * mm});
            skLineSegment(sketch, "E333", {"start": v(25.24, 7.96) * mm, "end": v(24.77, 7.96) * mm});
            skLineSegment(sketch, "E334", {"start": v(-3.67, -7.7) * mm, "end": v(-3.48, -7.82) * mm});
            skLineSegment(sketch, "E335", {"start": v(-3.48, -7.82) * mm, "end": v(-2.87, -8.1) * mm});
            skLineSegment(sketch, "E336", {"start": v(-2.87, -8.1) * mm, "end": v(-1.89, -8.46) * mm});
            skLineSegment(sketch, "E337", {"start": v(-1.89, -8.46) * mm, "end": v(-0.8, -8.7) * mm});
            skLineSegment(sketch, "E338", {"start": v(-0.8, -8.7) * mm, "end": v(0.02, -8.8) * mm});
            skLineSegment(sketch, "E339", {"start": v(0.02, -8.8) * mm, "end": v(0.3, -8.8) * mm});
            skLineSegment(sketch, "E340", {"start": v(0.3, -8.8) * mm, "end": v(0.6, -8.8) * mm});
            skLineSegment(sketch, "E341", {"start": v(0.6, -8.8) * mm, "end": v(1.53, -8.68) * mm});
            skLineSegment(sketch, "E342", {"start": v(1.53, -8.68) * mm, "end": v(2.36, -8.33) * mm});
            skLineSegment(sketch, "E343", {"start": v(2.36, -8.33) * mm, "end": v(2.84, -7.77) * mm});
            skLineSegment(sketch, "E344", {"start": v(2.84, -7.77) * mm, "end": v(2.99, -7.2) * mm});
            skLineSegment(sketch, "E345", {"start": v(2.99, -7.2) * mm, "end": v(2.99, -7) * mm});
            skLineSegment(sketch, "E346", {"start": v(2.99, -7) * mm, "end": v(2.99, -6.8) * mm});
            skLineSegment(sketch, "E347", {"start": v(2.99, -6.8) * mm, "end": v(2.86, -6.21) * mm});
            skLineSegment(sketch, "E348", {"start": v(2.86, -6.21) * mm, "end": v(2.42, -5.6) * mm});
            skLineSegment(sketch, "E349", {"start": v(2.42, -5.6) * mm, "end": v(1.6, -5.07) * mm});
            skLineSegment(sketch, "E350", {"start": v(1.6, -5.07) * mm, "end": v(0.64, -4.66) * mm});
            skLineSegment(sketch, "E351", {"start": v(0.64, -4.66) * mm, "end": v(0.32, -4.54) * mm});
            skLineSegment(sketch, "E352", {"start": v(0.32, -4.54) * mm, "end": v(-0.19, -4.37) * mm});
            skLineSegment(sketch, "E353", {"start": v(-0.19, -4.37) * mm, "end": v(-1.63, -3.62) * mm});
            skLineSegment(sketch, "E354", {"start": v(-1.63, -3.62) * mm, "end": v(-2.97, -2.5) * mm});
            skLineSegment(sketch, "E355", {"start": v(-2.97, -2.5) * mm, "end": v(-3.76, -1.2) * mm});
            skLineSegment(sketch, "E356", {"start": v(-3.76, -1.2) * mm, "end": v(-4.01, -0.17) * mm});
            skLineSegment(sketch, "E357", {"start": v(-4.01, -0.17) * mm, "end": v(-4.01, 0.17) * mm});
            skLineSegment(sketch, "E358", {"start": v(-4.01, 0.17) * mm, "end": v(-4.01, 0.65) * mm});
            skLineSegment(sketch, "E359", {"start": v(-4.01, 0.65) * mm, "end": v(-3.6, 2.09) * mm});
            skLineSegment(sketch, "E360", {"start": v(-3.6, 2.09) * mm, "end": v(-2.44, 3.66) * mm});
            skLineSegment(sketch, "E361", {"start": v(-2.44, 3.66) * mm, "end": v(-0.6, 4.73) * mm});
            skLineSegment(sketch, "E362", {"start": v(-0.6, 4.73) * mm, "end": v(1.23, 5.12) * mm});
            skLineSegment(sketch, "E363", {"start": v(1.23, 5.12) * mm, "end": v(1.83, 5.12) * mm});
            skLineSegment(sketch, "E364", {"start": v(1.83, 5.12) * mm, "end": v(2.14, 5.12) * mm});
            skLineSegment(sketch, "E365", {"start": v(2.14, 5.12) * mm, "end": v(3.07, 5.03) * mm});
            skLineSegment(sketch, "E366", {"start": v(3.07, 5.03) * mm, "end": v(4.19, 4.8) * mm});
            skLineSegment(sketch, "E367", {"start": v(4.19, 4.8) * mm, "end": v(5.16, 4.46) * mm});
            skLineSegment(sketch, "E368", {"start": v(5.16, 4.46) * mm, "end": v(5.76, 4.19) * mm});
            skLineSegment(sketch, "E369", {"start": v(5.76, 4.19) * mm, "end": v(5.95, 4.08) * mm});
            skLineSegment(sketch, "E370", {"start": v(5.95, 4.08) * mm, "end": v(5.18, 1.47) * mm});
            skLineSegment(sketch, "E371", {"start": v(5.18, 1.47) * mm, "end": v(4.96, 1.57) * mm});
            skLineSegment(sketch, "E372", {"start": v(4.96, 1.57) * mm, "end": v(3.73, 2) * mm});
            skLineSegment(sketch, "E373", {"start": v(3.73, 2) * mm, "end": v(2.2, 2.22) * mm});
            skLineSegment(sketch, "E374", {"start": v(2.2, 2.22) * mm, "end": v(1.83, 2.22) * mm});
            skLineSegment(sketch, "E375", {"start": v(1.83, 2.22) * mm, "end": v(1.6, 2.22) * mm});
            skLineSegment(sketch, "E376", {"start": v(1.6, 2.22) * mm, "end": v(0.88, 2.09) * mm});
            skLineSegment(sketch, "E377", {"start": v(0.88, 2.09) * mm, "end": v(0.23, 1.74) * mm});
            skLineSegment(sketch, "E378", {"start": v(0.23, 1.74) * mm, "end": v(-0.14, 1.22) * mm});
            skLineSegment(sketch, "E379", {"start": v(-0.14, 1.22) * mm, "end": v(-0.26, 0.72) * mm});
            skLineSegment(sketch, "E380", {"start": v(-0.26, 0.72) * mm, "end": v(-0.26, 0.56) * mm});
            skLineSegment(sketch, "E381", {"start": v(-0.26, 0.56) * mm, "end": v(-0.26, 0.37) * mm});
            skLineSegment(sketch, "E382", {"start": v(-0.26, 0.37) * mm, "end": v(-0.06, -0.2) * mm});
            skLineSegment(sketch, "E383", {"start": v(-0.06, -0.2) * mm, "end": v(0.5, -0.8) * mm});
            skLineSegment(sketch, "E384", {"start": v(0.5, -0.8) * mm, "end": v(1.31, -1.28) * mm});
            skLineSegment(sketch, "E385", {"start": v(1.31, -1.28) * mm, "end": v(2.07, -1.6) * mm});
            skLineSegment(sketch, "E386", {"start": v(2.07, -1.6) * mm, "end": v(2.33, -1.69) * mm});
            skLineSegment(sketch, "E387", {"start": v(2.33, -1.69) * mm, "end": v(2.82, -1.85) * mm});
            skLineSegment(sketch, "E388", {"start": v(2.82, -1.85) * mm, "end": v(4.23, -2.53) * mm});
            skLineSegment(sketch, "E389", {"start": v(4.23, -2.53) * mm, "end": v(5.61, -3.64) * mm});
            skLineSegment(sketch, "E390", {"start": v(5.61, -3.64) * mm, "end": v(6.46, -5.02) * mm});
            skLineSegment(sketch, "E391", {"start": v(6.46, -5.02) * mm, "end": v(6.74, -6.28) * mm});
            skLineSegment(sketch, "E392", {"start": v(6.74, -6.28) * mm, "end": v(6.74, -6.7) * mm});
            skLineSegment(sketch, "E393", {"start": v(6.74, -6.7) * mm, "end": v(6.74, -7.2) * mm});
            skLineSegment(sketch, "E394", {"start": v(6.74, -7.2) * mm, "end": v(6.3, -8.7) * mm});
            skLineSegment(sketch, "E395", {"start": v(6.3, -8.7) * mm, "end": v(5.01, -10.28) * mm});
            skLineSegment(sketch, "E396", {"start": v(5.01, -10.28) * mm, "end": v(2.98, -11.32) * mm});
            skLineSegment(sketch, "E397", {"start": v(2.98, -11.32) * mm, "end": v(0.93, -11.7) * mm});
            skLineSegment(sketch, "E398", {"start": v(0.93, -11.7) * mm, "end": v(0.26, -11.7) * mm});
            skLineSegment(sketch, "E399", {"start": v(0.26, -11.7) * mm, "end": v(-0.08, -11.7) * mm});
            skLineSegment(sketch, "E400", {"start": v(-0.08, -11.7) * mm, "end": v(-1.1, -11.62) * mm});
            skLineSegment(sketch, "E401", {"start": v(-1.1, -11.62) * mm, "end": v(-2.36, -11.4) * mm});
            skLineSegment(sketch, "E402", {"start": v(-2.36, -11.4) * mm, "end": v(-3.5, -11.02) * mm});
            skLineSegment(sketch, "E403", {"start": v(-3.5, -11.02) * mm, "end": v(-4.22, -10.64) * mm});
            skLineSegment(sketch, "E404", {"start": v(-4.22, -10.64) * mm, "end": v(-4.44, -10.48) * mm});
            skLineSegment(sketch, "E405", {"start": v(-4.44, -10.48) * mm, "end": v(-3.67, -7.7) * mm});
            skLineSegment(sketch, "E406", {"start": v(79.4, -10.77) * mm, "end": v(79.21, -10.86) * mm});
            skLineSegment(sketch, "E407", {"start": v(79.21, -10.86) * mm, "end": v(78.63, -11.07) * mm});
            skLineSegment(sketch, "E408", {"start": v(78.63, -11.07) * mm, "end": v(77.59, -11.36) * mm});
            skLineSegment(sketch, "E409", {"start": v(77.59, -11.36) * mm, "end": v(76.3, -11.57) * mm});
            skLineSegment(sketch, "E410", {"start": v(76.3, -11.57) * mm, "end": v(75.21, -11.65) * mm});
            skLineSegment(sketch, "E411", {"start": v(75.21, -11.65) * mm, "end": v(74.85, -11.65) * mm});
            skLineSegment(sketch, "E412", {"start": v(74.85, -11.65) * mm, "end": v(74.04, -11.64) * mm});
            skLineSegment(sketch, "E413", {"start": v(74.04, -11.64) * mm, "end": v(71.6, -11.05) * mm});
            skLineSegment(sketch, "E414", {"start": v(71.6, -11.05) * mm, "end": v(69.02, -9.4) * mm});
            skLineSegment(sketch, "E415", {"start": v(69.02, -9.4) * mm, "end": v(67.32, -6.82) * mm});
            skLineSegment(sketch, "E416", {"start": v(67.32, -6.82) * mm, "end": v(66.7, -4.3) * mm});
            skLineSegment(sketch, "E417", {"start": v(66.7, -4.3) * mm, "end": v(66.7, -3.46) * mm});
            skLineSegment(sketch, "E418", {"start": v(66.7, -3.46) * mm, "end": v(66.7, -2.61) * mm});
            skLineSegment(sketch, "E419", {"start": v(66.7, -2.61) * mm, "end": v(67.28, -0.08) * mm});
            skLineSegment(sketch, "E420", {"start": v(67.28, -0.08) * mm, "end": v(68.97, 2.63) * mm});
            skLineSegment(sketch, "E421", {"start": v(68.97, 2.63) * mm, "end": v(71.72, 4.44) * mm});
            skLineSegment(sketch, "E422", {"start": v(71.72, 4.44) * mm, "end": v(74.53, 5.1) * mm});
            skLineSegment(sketch, "E423", {"start": v(74.53, 5.1) * mm, "end": v(75.47, 5.1) * mm});
            skLineSegment(sketch, "E424", {"start": v(75.47, 5.1) * mm, "end": v(75.76, 5.1) * mm});
            skLineSegment(sketch, "E425", {"start": v(75.76, 5.1) * mm, "end": v(76.64, 5.03) * mm});
            skLineSegment(sketch, "E426", {"start": v(76.64, 5.03) * mm, "end": v(77.73, 4.84) * mm});
            skLineSegment(sketch, "E427", {"start": v(77.73, 4.84) * mm, "end": v(78.67, 4.57) * mm});
            skLineSegment(sketch, "E428", {"start": v(78.67, 4.57) * mm, "end": v(79.25, 4.35) * mm});
            skLineSegment(sketch, "E429", {"start": v(79.25, 4.35) * mm, "end": v(79.44, 4.27) * mm});
            skLineSegment(sketch, "E430", {"start": v(79.44, 4.27) * mm, "end": v(78.76, 1.43) * mm});
            skLineSegment(sketch, "E431", {"start": v(78.76, 1.43) * mm, "end": v(78.59, 1.52) * mm});
            skLineSegment(sketch, "E432", {"start": v(78.59, 1.52) * mm, "end": v(77.47, 1.84) * mm});
            skLineSegment(sketch, "E433", {"start": v(77.47, 1.84) * mm, "end": v(76.03, 1.98) * mm});
            skLineSegment(sketch, "E434", {"start": v(76.03, 1.98) * mm, "end": v(75.56, 1.98) * mm});
            skLineSegment(sketch, "E435", {"start": v(75.56, 1.98) * mm, "end": v(75.26, 1.98) * mm});
            skLineSegment(sketch, "E436", {"start": v(75.26, 1.98) * mm, "end": v(74.4, 1.89) * mm});
            skLineSegment(sketch, "E437", {"start": v(74.4, 1.89) * mm, "end": v(73.4, 1.6) * mm});
            skLineSegment(sketch, "E438", {"start": v(73.4, 1.6) * mm, "end": v(72.56, 1.13) * mm});
            skLineSegment(sketch, "E439", {"start": v(72.56, 1.13) * mm, "end": v(71.88, 0.5) * mm});
            skLineSegment(sketch, "E440", {"start": v(71.88, 0.5) * mm, "end": v(71.36, -0.26) * mm});
            skLineSegment(sketch, "E441", {"start": v(71.36, -0.26) * mm, "end": v(71, -1.16) * mm});
            skLineSegment(sketch, "E442", {"start": v(71, -1.16) * mm, "end": v(70.78, -2.17) * mm});
            skLineSegment(sketch, "E443", {"start": v(70.78, -2.17) * mm, "end": v(70.7, -3) * mm});
            skLineSegment(sketch, "E444", {"start": v(70.7, -3) * mm, "end": v(70.71, -3.29) * mm});
            skLineSegment(sketch, "E445", {"start": v(70.71, -3.29) * mm, "end": v(70.71, -3.6) * mm});
            skLineSegment(sketch, "E446", {"start": v(70.71, -3.6) * mm, "end": v(70.8, -4.5) * mm});
            skLineSegment(sketch, "E447", {"start": v(70.8, -4.5) * mm, "end": v(71.05, -5.58) * mm});
            skLineSegment(sketch, "E448", {"start": v(71.05, -5.58) * mm, "end": v(71.47, -6.5) * mm});
            skLineSegment(sketch, "E449", {"start": v(71.47, -6.5) * mm, "end": v(72.03, -7.27) * mm});
            skLineSegment(sketch, "E450", {"start": v(72.03, -7.27) * mm, "end": v(72.72, -7.87) * mm});
            skLineSegment(sketch, "E451", {"start": v(72.72, -7.87) * mm, "end": v(73.55, -8.3) * mm});
            skLineSegment(sketch, "E452", {"start": v(73.55, -8.3) * mm, "end": v(74.49, -8.57) * mm});
            skLineSegment(sketch, "E453", {"start": v(74.49, -8.57) * mm, "end": v(75.27, -8.66) * mm});
            skLineSegment(sketch, "E454", {"start": v(75.27, -8.66) * mm, "end": v(75.53, -8.66) * mm});
            skLineSegment(sketch, "E455", {"start": v(75.53, -8.66) * mm, "end": v(76.01, -8.66) * mm});
            skLineSegment(sketch, "E456", {"start": v(76.01, -8.66) * mm, "end": v(77.46, -8.45) * mm});
            skLineSegment(sketch, "E457", {"start": v(77.46, -8.45) * mm, "end": v(78.67, -8.07) * mm});
            skLineSegment(sketch, "E458", {"start": v(78.67, -8.07) * mm, "end": v(78.86, -7.98) * mm});
            skLineSegment(sketch, "E459", {"start": v(78.86, -7.98) * mm, "end": v(79.4, -10.77) * mm});
            skLineSegment(sketch, "E460", {"start": v(84.03, -4.2) * mm, "end": v(84.03, -4.49) * mm});
            skLineSegment(sketch, "E461", {"start": v(84.03, -4.49) * mm, "end": v(84.15, -5.35) * mm});
            skLineSegment(sketch, "E462", {"start": v(84.15, -5.35) * mm, "end": v(84.44, -6.3) * mm});
            skLineSegment(sketch, "E463", {"start": v(84.44, -6.3) * mm, "end": v(84.88, -7.07) * mm});
            skLineSegment(sketch, "E464", {"start": v(84.88, -7.07) * mm, "end": v(85.45, -7.69) * mm});
            skLineSegment(sketch, "E465", {"start": v(85.45, -7.69) * mm, "end": v(86.15, -8.14) * mm});
            skLineSegment(sketch, "E466", {"start": v(86.15, -8.14) * mm, "end": v(86.96, -8.45) * mm});
            skLineSegment(sketch, "E467", {"start": v(86.96, -8.45) * mm, "end": v(87.86, -8.63) * mm});
            skLineSegment(sketch, "E468", {"start": v(87.86, -8.63) * mm, "end": v(88.6, -8.69) * mm});
            skLineSegment(sketch, "E469", {"start": v(88.6, -8.69) * mm, "end": v(88.85, -8.69) * mm});
            skLineSegment(sketch, "E470", {"start": v(88.85, -8.69) * mm, "end": v(89.48, -8.69) * mm});
            skLineSegment(sketch, "E471", {"start": v(89.48, -8.69) * mm, "end": v(91.35, -8.47) * mm});
            skLineSegment(sketch, "E472", {"start": v(91.35, -8.47) * mm, "end": v(92.98, -8.03) * mm});
            skLineSegment(sketch, "E473", {"start": v(92.98, -8.03) * mm, "end": v(93.27, -7.92) * mm});
            skLineSegment(sketch, "E474", {"start": v(93.27, -7.92) * mm, "end": v(93.84, -10.6) * mm});
            skLineSegment(sketch, "E475", {"start": v(93.84, -10.6) * mm, "end": v(93.58, -10.71) * mm});
            skLineSegment(sketch, "E476", {"start": v(93.58, -10.71) * mm, "end": v(92.8, -11) * mm});
            skLineSegment(sketch, "E477", {"start": v(92.8, -11) * mm, "end": v(91.53, -11.37) * mm});
            skLineSegment(sketch, "E478", {"start": v(91.53, -11.37) * mm, "end": v(90.04, -11.63) * mm});
            skLineSegment(sketch, "E479", {"start": v(90.04, -11.63) * mm, "end": v(88.76, -11.74) * mm});
            skLineSegment(sketch, "E480", {"start": v(88.76, -11.74) * mm, "end": v(88.34, -11.74) * mm});
            skLineSegment(sketch, "E481", {"start": v(88.34, -11.74) * mm, "end": v(87.48, -11.74) * mm});
            skLineSegment(sketch, "E482", {"start": v(87.48, -11.74) * mm, "end": v(84.93, -11.14) * mm});
            skLineSegment(sketch, "E483", {"start": v(84.93, -11.14) * mm, "end": v(82.38, -9.45) * mm});
            skLineSegment(sketch, "E484", {"start": v(82.38, -9.45) * mm, "end": v(80.78, -6.86) * mm});
            skLineSegment(sketch, "E485", {"start": v(80.78, -6.86) * mm, "end": v(80.23, -4.35) * mm});
            skLineSegment(sketch, "E486", {"start": v(80.23, -4.35) * mm, "end": v(80.23, -3.52) * mm});
            skLineSegment(sketch, "E487", {"start": v(80.23, -3.52) * mm, "end": v(80.23, -2.7) * mm});
            skLineSegment(sketch, "E488", {"start": v(80.23, -2.7) * mm, "end": v(80.73, -0.25) * mm});
            skLineSegment(sketch, "E489", {"start": v(80.73, -0.25) * mm, "end": v(82.23, 2.5) * mm});
            skLineSegment(sketch, "E490", {"start": v(82.23, 2.5) * mm, "end": v(84.65, 4.38) * mm});
            skLineSegment(sketch, "E491", {"start": v(84.65, 4.38) * mm, "end": v(87.13, 5.08) * mm});
            skLineSegment(sketch, "E492", {"start": v(87.13, 5.08) * mm, "end": v(87.95, 5.08) * mm});
            skLineSegment(sketch, "E493", {"start": v(87.95, 5.08) * mm, "end": v(88.4, 5.08) * mm});
            skLineSegment(sketch, "E494", {"start": v(88.4, 5.08) * mm, "end": v(89.74, 4.88) * mm});
            skLineSegment(sketch, "E495", {"start": v(89.74, 4.88) * mm, "end": v(91.2, 4.34) * mm});
            skLineSegment(sketch, "E496", {"start": v(91.2, 4.34) * mm, "end": v(92.39, 3.52) * mm});
            skLineSegment(sketch, "E497", {"start": v(92.39, 3.52) * mm, "end": v(93.3, 2.47) * mm});
            skLineSegment(sketch, "E498", {"start": v(93.3, 2.47) * mm, "end": v(93.96, 1.28) * mm});
            skLineSegment(sketch, "E499", {"start": v(93.96, 1.28) * mm, "end": v(94.4, 0) * mm});
            skLineSegment(sketch, "E500", {"start": v(94.4, 0) * mm, "end": v(94.66, -1.31) * mm});
            skLineSegment(sketch, "E501", {"start": v(94.66, -1.31) * mm, "end": v(94.74, -2.27) * mm});
            skLineSegment(sketch, "E502", {"start": v(94.74, -2.27) * mm, "end": v(94.74, -2.58) * mm});
            skLineSegment(sketch, "E503", {"start": v(94.74, -2.58) * mm, "end": v(94.74, -2.81) * mm});
            skLineSegment(sketch, "E504", {"start": v(94.74, -2.81) * mm, "end": v(94.73, -3.5) * mm});
            skLineSegment(sketch, "E505", {"start": v(94.73, -3.5) * mm, "end": v(94.67, -4.09) * mm});
            skLineSegment(sketch, "E506", {"start": v(94.67, -4.09) * mm, "end": v(94.65, -4.18) * mm});
            skLineSegment(sketch, "E507", {"start": v(94.65, -4.18) * mm, "end": v(84.03, -4.2) * mm});
            skLineSegment(sketch, "E508", {"start": v(91.09, -1.45) * mm, "end": v(91.1, -1.3) * mm});
            skLineSegment(sketch, "E509", {"start": v(91.1, -1.3) * mm, "end": v(91.07, -0.83) * mm});
            skLineSegment(sketch, "E510", {"start": v(91.07, -0.83) * mm, "end": v(90.98, -0.19) * mm});
            skLineSegment(sketch, "E511", {"start": v(90.98, -0.19) * mm, "end": v(90.8, 0.44) * mm});
            skLineSegment(sketch, "E512", {"start": v(90.8, 0.44) * mm, "end": v(90.5, 1.03) * mm});
            skLineSegment(sketch, "E513", {"start": v(90.5, 1.03) * mm, "end": v(90.07, 1.54) * mm});
            skLineSegment(sketch, "E514", {"start": v(90.07, 1.54) * mm, "end": v(89.48, 1.94) * mm});
            skLineSegment(sketch, "E515", {"start": v(89.48, 1.94) * mm, "end": v(88.7, 2.2) * mm});
            skLineSegment(sketch, "E516", {"start": v(88.7, 2.2) * mm, "end": v(87.96, 2.3) * mm});
            skLineSegment(sketch, "E517", {"start": v(87.96, 2.3) * mm, "end": v(87.72, 2.3) * mm});
            skLineSegment(sketch, "E518", {"start": v(87.72, 2.3) * mm, "end": v(87.49, 2.3) * mm});
            skLineSegment(sketch, "E519", {"start": v(87.49, 2.3) * mm, "end": v(86.8, 2.22) * mm});
            skLineSegment(sketch, "E520", {"start": v(86.8, 2.22) * mm, "end": v(86.04, 1.97) * mm});
            skLineSegment(sketch, "E521", {"start": v(86.04, 1.97) * mm, "end": v(85.42, 1.58) * mm});
            skLineSegment(sketch, "E522", {"start": v(85.42, 1.58) * mm, "end": v(84.95, 1.1) * mm});
            skLineSegment(sketch, "E523", {"start": v(84.95, 1.1) * mm, "end": v(84.58, 0.52) * mm});
            skLineSegment(sketch, "E524", {"start": v(84.58, 0.52) * mm, "end": v(84.32, -0.12) * mm});
            skLineSegment(sketch, "E525", {"start": v(84.32, -0.12) * mm, "end": v(84.15, -0.78) * mm});
            skLineSegment(sketch, "E526", {"start": v(84.15, -0.78) * mm, "end": v(84.07, -1.28) * mm});
            skLineSegment(sketch, "E527", {"start": v(84.07, -1.28) * mm, "end": v(84.05, -1.45) * mm});
            skLineSegment(sketch, "E528", {"start": v(84.05, -1.45) * mm, "end": v(91.09, -1.45) * mm});
            skLineSegment(sketch, "E529", {"start": v(-92.4, 13.96) * mm, "end": v(-92.4, 18.27) * mm});
            skLineSegment(sketch, "E530", {"start": v(-92.4, 18.27) * mm, "end": v(-92.4, 18.4) * mm});
            skLineSegment(sketch, "E531", {"start": v(-92.4, 18.4) * mm, "end": v(-92.28, 18.84) * mm});
            skLineSegment(sketch, "E532", {"start": v(-92.28, 18.84) * mm, "end": v(-91.96, 19.3) * mm});
            skLineSegment(sketch, "E533", {"start": v(-91.96, 19.3) * mm, "end": v(-91.5, 19.62) * mm});
            skLineSegment(sketch, "E534", {"start": v(-91.5, 19.62) * mm, "end": v(-91.06, 19.74) * mm});
            skLineSegment(sketch, "E535", {"start": v(-91.06, 19.74) * mm, "end": v(-90.92, 19.74) * mm});
            skLineSegment(sketch, "E536", {"start": v(-90.92, 19.74) * mm, "end": v(-71.52, 19.74) * mm});
            skLineSegment(sketch, "E537", {"start": v(-71.52, 19.74) * mm, "end": v(-71.38, 19.74) * mm});
            skLineSegment(sketch, "E538", {"start": v(-71.38, 19.74) * mm, "end": v(-70.94, 19.62) * mm});
            skLineSegment(sketch, "E539", {"start": v(-70.94, 19.62) * mm, "end": v(-70.47, 19.3) * mm});
            skLineSegment(sketch, "E540", {"start": v(-70.47, 19.3) * mm, "end": v(-70.15, 18.84) * mm});
            skLineSegment(sketch, "E541", {"start": v(-70.15, 18.84) * mm, "end": v(-70.03, 18.4) * mm});
            skLineSegment(sketch, "E542", {"start": v(-70.03, 18.4) * mm, "end": v(-70.03, 18.27) * mm});
            skLineSegment(sketch, "E543", {"start": v(-70.03, 18.27) * mm, "end": v(-70.03, 13.96) * mm});
            skLineSegment(sketch, "E544", {"start": v(-70.03, 13.96) * mm, "end": v(-92.4, 13.96) * mm});
            skLineSegment(sketch, "E545", {"start": v(-92.4, 12.9) * mm, "end": v(-70.03, 12.9) * mm});
            skLineSegment(sketch, "E546", {"start": v(-70.03, 12.9) * mm, "end": v(-70.03, -12.9) * mm});
            skLineSegment(sketch, "E547", {"start": v(-70.03, -12.9) * mm, "end": v(-92.4, -12.9) * mm});
            skLineSegment(sketch, "E548", {"start": v(-92.4, -12.9) * mm, "end": v(-92.4, 12.9) * mm});
            skLineSegment(sketch, "E549", {"start": v(-74.75, 16.07) * mm, "end": v(-74.72, 16.03) * mm});
            skLineSegment(sketch, "E550", {"start": v(-74.72, 16.03) * mm, "end": v(-74.37, 15.74) * mm});
            skLineSegment(sketch, "E551", {"start": v(-74.37, 15.74) * mm, "end": v(-74.34, 15.73) * mm});
            skLineSegment(sketch, "E552", {"start": v(-74.34, 15.73) * mm, "end": v(-74.25, 15.68) * mm});
            skLineSegment(sketch, "E553", {"start": v(-74.25, 15.68) * mm, "end": v(-73.55, 15.47) * mm});
            skLineSegment(sketch, "E554", {"start": v(-73.55, 15.47) * mm, "end": v(-73.32, 15.47) * mm});
            skLineSegment(sketch, "E555", {"start": v(-73.32, 15.47) * mm, "end": v(-73.16, 15.47) * mm});
            skLineSegment(sketch, "E556", {"start": v(-73.16, 15.47) * mm, "end": v(-72.69, 15.63) * mm});
            skLineSegment(sketch, "E557", {"start": v(-72.69, 15.63) * mm, "end": v(-72.46, 15.94) * mm});
            skLineSegment(sketch, "E558", {"start": v(-72.46, 15.94) * mm, "end": v(-72.46, 16.05) * mm});
            skLineSegment(sketch, "E559", {"start": v(-72.46, 16.05) * mm, "end": v(-72.46, 16.15) * mm});
            skLineSegment(sketch, "E560", {"start": v(-72.46, 16.15) * mm, "end": v(-72.74, 16.44) * mm});
            skLineSegment(sketch, "E561", {"start": v(-72.74, 16.44) * mm, "end": v(-73.33, 16.58) * mm});
            skLineSegment(sketch, "E562", {"start": v(-73.33, 16.58) * mm, "end": v(-73.49, 16.6) * mm});
            skLineSegment(sketch, "E563", {"start": v(-73.49, 16.6) * mm, "end": v(-73.68, 16.63) * mm});
            skLineSegment(sketch, "E564", {"start": v(-73.68, 16.63) * mm, "end": v(-74.4, 16.96) * mm});
            skLineSegment(sketch, "E565", {"start": v(-74.4, 16.96) * mm, "end": v(-74.7, 17.52) * mm});
            skLineSegment(sketch, "E566", {"start": v(-74.7, 17.52) * mm, "end": v(-74.7, 17.71) * mm});
            skLineSegment(sketch, "E567", {"start": v(-74.7, 17.71) * mm, "end": v(-74.7, 17.82) * mm});
            skLineSegment(sketch, "E568", {"start": v(-74.7, 17.82) * mm, "end": v(-74.58, 18.16) * mm});
            skLineSegment(sketch, "E569", {"start": v(-74.58, 18.16) * mm, "end": v(-74.28, 18.52) * mm});
            skLineSegment(sketch, "E570", {"start": v(-74.28, 18.52) * mm, "end": v(-73.8, 18.76) * mm});
            skLineSegment(sketch, "E571", {"start": v(-73.8, 18.76) * mm, "end": v(-73.36, 18.84) * mm});
            skLineSegment(sketch, "E572", {"start": v(-73.36, 18.84) * mm, "end": v(-73.2, 18.84) * mm});
            skLineSegment(sketch, "E573", {"start": v(-73.2, 18.84) * mm, "end": v(-73.02, 18.84) * mm});
            skLineSegment(sketch, "E574", {"start": v(-73.02, 18.84) * mm, "end": v(-72.45, 18.76) * mm});
            skLineSegment(sketch, "E575", {"start": v(-72.45, 18.76) * mm, "end": v(-72.01, 18.62) * mm});
            skLineSegment(sketch, "E576", {"start": v(-72.01, 18.62) * mm, "end": v(-71.95, 18.59) * mm});
            skLineSegment(sketch, "E577", {"start": v(-71.95, 18.59) * mm, "end": v(-71.95, 17.75) * mm});
            skLineSegment(sketch, "E578", {"start": v(-71.95, 17.75) * mm, "end": v(-71.97, 17.8) * mm});
            skLineSegment(sketch, "E579", {"start": v(-71.97, 17.8) * mm, "end": v(-72.37, 18.07) * mm});
            skLineSegment(sketch, "E580", {"start": v(-72.37, 18.07) * mm, "end": v(-72.42, 18.1) * mm});
            skLineSegment(sketch, "E581", {"start": v(-72.42, 18.1) * mm, "end": v(-72.48, 18.12) * mm});
            skLineSegment(sketch, "E582", {"start": v(-72.48, 18.12) * mm, "end": v(-73.03, 18.22) * mm});
            skLineSegment(sketch, "E583", {"start": v(-73.03, 18.22) * mm, "end": v(-73.2, 18.22) * mm});
            skLineSegment(sketch, "E584", {"start": v(-73.2, 18.22) * mm, "end": v(-73.33, 18.22) * mm});
            skLineSegment(sketch, "E585", {"start": v(-73.33, 18.22) * mm, "end": v(-73.71, 18.11) * mm});
            skLineSegment(sketch, "E586", {"start": v(-73.71, 18.11) * mm, "end": v(-73.9, 17.9) * mm});
            skLineSegment(sketch, "E587", {"start": v(-73.9, 17.9) * mm, "end": v(-73.9, 17.84) * mm});
            skLineSegment(sketch, "E588", {"start": v(-73.9, 17.84) * mm, "end": v(-73.9, 17.75) * mm});
            skLineSegment(sketch, "E589", {"start": v(-73.9, 17.75) * mm, "end": v(-73.63, 17.48) * mm});
            skLineSegment(sketch, "E590", {"start": v(-73.63, 17.48) * mm, "end": v(-73, 17.32) * mm});
            skLineSegment(sketch, "E591", {"start": v(-73, 17.32) * mm, "end": v(-72.8, 17.28) * mm});
            skLineSegment(sketch, "E592", {"start": v(-72.8, 17.28) * mm, "end": v(-72.62, 17.25) * mm});
            skLineSegment(sketch, "E593", {"start": v(-72.62, 17.25) * mm, "end": v(-71.93, 16.91) * mm});
            skLineSegment(sketch, "E594", {"start": v(-71.93, 16.91) * mm, "end": v(-71.63, 16.32) * mm});
            skLineSegment(sketch, "E595", {"start": v(-71.63, 16.32) * mm, "end": v(-71.63, 16.15) * mm});
            skLineSegment(sketch, "E596", {"start": v(-71.63, 16.15) * mm, "end": v(-71.63, 16.02) * mm});
            skLineSegment(sketch, "E597", {"start": v(-71.63, 16.02) * mm, "end": v(-71.75, 15.63) * mm});
            skLineSegment(sketch, "E598", {"start": v(-71.75, 15.63) * mm, "end": v(-72.08, 15.22) * mm});
            skLineSegment(sketch, "E599", {"start": v(-72.08, 15.22) * mm, "end": v(-72.6, 14.96) * mm});
            skLineSegment(sketch, "E600", {"start": v(-72.6, 14.96) * mm, "end": v(-73.14, 14.87) * mm});
            skLineSegment(sketch, "E601", {"start": v(-73.14, 14.87) * mm, "end": v(-73.32, 14.87) * mm});
            skLineSegment(sketch, "E602", {"start": v(-73.32, 14.87) * mm, "end": v(-73.5, 14.87) * mm});
            skLineSegment(sketch, "E603", {"start": v(-73.5, 14.87) * mm, "end": v(-74.07, 14.94) * mm});
            skLineSegment(sketch, "E604", {"start": v(-74.07, 14.94) * mm, "end": v(-74.66, 15.1) * mm});
            skLineSegment(sketch, "E605", {"start": v(-74.66, 15.1) * mm, "end": v(-74.75, 15.15) * mm});
            skLineSegment(sketch, "E606", {"start": v(-74.75, 15.15) * mm, "end": v(-74.75, 16.07) * mm});
            skLineSegment(sketch, "E607", {"start": v(-87.44, 15.9) * mm, "end": v(-87.49, 15.99) * mm});
            skLineSegment(sketch, "E608", {"start": v(-87.49, 15.99) * mm, "end": v(-87.72, 16.37) * mm});
            skLineSegment(sketch, "E609", {"start": v(-87.72, 16.37) * mm, "end": v(-88, 16.63) * mm});
            skLineSegment(sketch, "E610", {"start": v(-88, 16.63) * mm, "end": v(-88.06, 16.66) * mm});
            skLineSegment(sketch, "E611", {"start": v(-88.06, 16.66) * mm, "end": v(-87.91, 16.7) * mm});
            skLineSegment(sketch, "E612", {"start": v(-87.91, 16.7) * mm, "end": v(-87.39, 17.01) * mm});
            skLineSegment(sketch, "E613", {"start": v(-87.39, 17.01) * mm, "end": v(-87.16, 17.49) * mm});
            skLineSegment(sketch, "E614", {"start": v(-87.16, 17.49) * mm, "end": v(-87.16, 17.65) * mm});
            skLineSegment(sketch, "E615", {"start": v(-87.16, 17.65) * mm, "end": v(-87.16, 17.8) * mm});
            skLineSegment(sketch, "E616", {"start": v(-87.16, 17.8) * mm, "end": v(-87.32, 18.29) * mm});
            skLineSegment(sketch, "E617", {"start": v(-87.32, 18.29) * mm, "end": v(-87.68, 18.63) * mm});
            skLineSegment(sketch, "E618", {"start": v(-87.68, 18.63) * mm, "end": v(-87.78, 18.67) * mm});
            skLineSegment(sketch, "E619", {"start": v(-87.78, 18.67) * mm, "end": v(-87.85, 18.7) * mm});
            skLineSegment(sketch, "E620", {"start": v(-87.85, 18.7) * mm, "end": v(-88.23, 18.76) * mm});
            skLineSegment(sketch, "E621", {"start": v(-88.23, 18.76) * mm, "end": v(-88.7, 18.78) * mm});
            skLineSegment(sketch, "E622", {"start": v(-88.7, 18.78) * mm, "end": v(-88.85, 18.78) * mm});
            skLineSegment(sketch, "E623", {"start": v(-88.85, 18.78) * mm, "end": v(-90.81, 18.78) * mm});
            skLineSegment(sketch, "E624", {"start": v(-90.81, 18.78) * mm, "end": v(-90.77, 18.75) * mm});
            skLineSegment(sketch, "E625", {"start": v(-90.77, 18.75) * mm, "end": v(-90.6, 18.43) * mm});
            skLineSegment(sketch, "E626", {"start": v(-90.6, 18.43) * mm, "end": v(-90.51, 18.05) * mm});
            skLineSegment(sketch, "E627", {"start": v(-90.51, 18.05) * mm, "end": v(-90.51, 17.92) * mm});
            skLineSegment(sketch, "E628", {"start": v(-90.51, 17.92) * mm, "end": v(-90.51, 15.77) * mm});
            skLineSegment(sketch, "E629", {"start": v(-90.51, 15.77) * mm, "end": v(-90.51, 15.64) * mm});
            skLineSegment(sketch, "E630", {"start": v(-90.51, 15.64) * mm, "end": v(-90.6, 15.27) * mm});
            skLineSegment(sketch, "E631", {"start": v(-90.6, 15.27) * mm, "end": v(-90.77, 14.96) * mm});
            skLineSegment(sketch, "E632", {"start": v(-90.77, 14.96) * mm, "end": v(-90.81, 14.94) * mm});
            skLineSegment(sketch, "E633", {"start": v(-90.81, 14.94) * mm, "end": v(-89.4, 14.94) * mm});
            skLineSegment(sketch, "E634", {"start": v(-89.4, 14.94) * mm, "end": v(-89.45, 14.96) * mm});
            skLineSegment(sketch, "E635", {"start": v(-89.45, 14.96) * mm, "end": v(-89.63, 15.27) * mm});
            skLineSegment(sketch, "E636", {"start": v(-89.63, 15.27) * mm, "end": v(-89.7, 15.64) * mm});
            skLineSegment(sketch, "E637", {"start": v(-89.7, 15.64) * mm, "end": v(-89.7, 15.77) * mm});
            skLineSegment(sketch, "E638", {"start": v(-89.7, 15.77) * mm, "end": v(-89.7, 16.45) * mm});
            skLineSegment(sketch, "E639", {"start": v(-89.7, 16.45) * mm, "end": v(-89.1, 16.45) * mm});
            skLineSegment(sketch, "E640", {"start": v(-89.1, 16.45) * mm, "end": v(-89.02, 16.45) * mm});
            skLineSegment(sketch, "E641", {"start": v(-89.02, 16.45) * mm, "end": v(-88.74, 16.37) * mm});
            skLineSegment(sketch, "E642", {"start": v(-88.74, 16.37) * mm, "end": v(-88.54, 16.17) * mm});
            skLineSegment(sketch, "E643", {"start": v(-88.54, 16.17) * mm, "end": v(-88.5, 16.11) * mm});
            skLineSegment(sketch, "E644", {"start": v(-88.5, 16.11) * mm, "end": v(-88.46, 16.03) * mm});
            skLineSegment(sketch, "E645", {"start": v(-88.46, 16.03) * mm, "end": v(-87.95, 15.03) * mm});
            skLineSegment(sketch, "E646", {"start": v(-87.95, 15.03) * mm, "end": v(-87.89, 14.94) * mm});
            skLineSegment(sketch, "E647", {"start": v(-87.89, 14.94) * mm, "end": v(-86.76, 14.94) * mm});
            skLineSegment(sketch, "E648", {"start": v(-86.76, 14.94) * mm, "end": v(-86.84, 15) * mm});
            skLineSegment(sketch, "E649", {"start": v(-86.84, 15) * mm, "end": v(-87.16, 15.37) * mm});
            skLineSegment(sketch, "E650", {"start": v(-87.16, 15.37) * mm, "end": v(-87.4, 15.8) * mm});
            skLineSegment(sketch, "E651", {"start": v(-87.4, 15.8) * mm, "end": v(-87.44, 15.9) * mm});
            skLineSegment(sketch, "E652", {"start": v(-88, 17.6) * mm, "end": v(-88, 17.5) * mm});
            skLineSegment(sketch, "E653", {"start": v(-88, 17.5) * mm, "end": v(-88.22, 17.2) * mm});
            skLineSegment(sketch, "E654", {"start": v(-88.22, 17.2) * mm, "end": v(-88.66, 17.07) * mm});
            skLineSegment(sketch, "E655", {"start": v(-88.66, 17.07) * mm, "end": v(-88.8, 17.07) * mm});
            skLineSegment(sketch, "E656", {"start": v(-88.8, 17.07) * mm, "end": v(-89.7, 17.07) * mm});
            skLineSegment(sketch, "E657", {"start": v(-89.7, 17.07) * mm, "end": v(-89.7, 18.16) * mm});
            skLineSegment(sketch, "E658", {"start": v(-89.7, 18.16) * mm, "end": v(-88.8, 18.16) * mm});
            skLineSegment(sketch, "E659", {"start": v(-88.8, 18.16) * mm, "end": v(-88.66, 18.16) * mm});
            skLineSegment(sketch, "E660", {"start": v(-88.66, 18.16) * mm, "end": v(-88.22, 18.03) * mm});
            skLineSegment(sketch, "E661", {"start": v(-88.22, 18.03) * mm, "end": v(-88, 17.71) * mm});
            skLineSegment(sketch, "E662", {"start": v(-88, 17.71) * mm, "end": v(-88, 17.6) * mm});
            skLineSegment(sketch, "E663", {"start": v(-85.27, 15.83) * mm, "end": v(-85.32, 15.89) * mm});
            skLineSegment(sketch, "E664", {"start": v(-85.32, 15.89) * mm, "end": v(-85.52, 16.25) * mm});
            skLineSegment(sketch, "E665", {"start": v(-85.52, 16.25) * mm, "end": v(-85.6, 16.7) * mm});
            skLineSegment(sketch, "E666", {"start": v(-85.6, 16.7) * mm, "end": v(-85.6, 16.86) * mm});
            skLineSegment(sketch, "E667", {"start": v(-85.6, 16.86) * mm, "end": v(-85.6, 17) * mm});
            skLineSegment(sketch, "E668", {"start": v(-85.6, 17) * mm, "end": v(-85.52, 17.45) * mm});
            skLineSegment(sketch, "E669", {"start": v(-85.52, 17.45) * mm, "end": v(-85.32, 17.82) * mm});
            skLineSegment(sketch, "E670", {"start": v(-85.32, 17.82) * mm, "end": v(-85.27, 17.88) * mm});
            skLineSegment(sketch, "E671", {"start": v(-85.27, 17.88) * mm, "end": v(-85.22, 17.93) * mm});
            skLineSegment(sketch, "E672", {"start": v(-85.22, 17.93) * mm, "end": v(-84.65, 18.2) * mm});
            skLineSegment(sketch, "E673", {"start": v(-84.65, 18.2) * mm, "end": v(-84.45, 18.2) * mm});
            skLineSegment(sketch, "E674", {"start": v(-84.45, 18.2) * mm, "end": v(-84.25, 18.2) * mm});
            skLineSegment(sketch, "E675", {"start": v(-84.25, 18.2) * mm, "end": v(-83.7, 17.93) * mm});
            skLineSegment(sketch, "E676", {"start": v(-83.7, 17.93) * mm, "end": v(-83.64, 17.88) * mm});
            skLineSegment(sketch, "E677", {"start": v(-83.64, 17.88) * mm, "end": v(-83.59, 17.82) * mm});
            skLineSegment(sketch, "E678", {"start": v(-83.59, 17.82) * mm, "end": v(-83.37, 17.45) * mm});
            skLineSegment(sketch, "E679", {"start": v(-83.37, 17.45) * mm, "end": v(-83.28, 17) * mm});
            skLineSegment(sketch, "E680", {"start": v(-83.28, 17) * mm, "end": v(-83.28, 16.86) * mm});
            skLineSegment(sketch, "E681", {"start": v(-83.28, 16.86) * mm, "end": v(-83.28, 16.7) * mm});
            skLineSegment(sketch, "E682", {"start": v(-83.28, 16.7) * mm, "end": v(-83.37, 16.25) * mm});
            skLineSegment(sketch, "E683", {"start": v(-83.37, 16.25) * mm, "end": v(-83.59, 15.89) * mm});
            skLineSegment(sketch, "E684", {"start": v(-83.59, 15.89) * mm, "end": v(-83.64, 15.83) * mm});
            skLineSegment(sketch, "E685", {"start": v(-83.64, 15.83) * mm, "end": v(-83.7, 15.78) * mm});
            skLineSegment(sketch, "E686", {"start": v(-83.7, 15.78) * mm, "end": v(-84.26, 15.51) * mm});
            skLineSegment(sketch, "E687", {"start": v(-84.26, 15.51) * mm, "end": v(-84.45, 15.51) * mm});
            skLineSegment(sketch, "E688", {"start": v(-84.45, 15.51) * mm, "end": v(-84.66, 15.51) * mm});
            skLineSegment(sketch, "E689", {"start": v(-84.66, 15.51) * mm, "end": v(-85.22, 15.78) * mm});
            skLineSegment(sketch, "E690", {"start": v(-85.22, 15.78) * mm, "end": v(-85.27, 15.83) * mm});
            skLineSegment(sketch, "E691", {"start": v(-84.45, 14.83) * mm, "end": v(-84.27, 14.83) * mm});
            skLineSegment(sketch, "E692", {"start": v(-84.27, 14.83) * mm, "end": v(-83.72, 14.94) * mm});
            skLineSegment(sketch, "E693", {"start": v(-83.72, 14.94) * mm, "end": v(-83.22, 15.2) * mm});
            skLineSegment(sketch, "E694", {"start": v(-83.22, 15.2) * mm, "end": v(-83.13, 15.28) * mm});
            skLineSegment(sketch, "E695", {"start": v(-83.13, 15.28) * mm, "end": v(-83.03, 15.36) * mm});
            skLineSegment(sketch, "E696", {"start": v(-83.03, 15.36) * mm, "end": v(-82.64, 15.92) * mm});
            skLineSegment(sketch, "E697", {"start": v(-82.64, 15.92) * mm, "end": v(-82.45, 16.62) * mm});
            skLineSegment(sketch, "E698", {"start": v(-82.45, 16.62) * mm, "end": v(-82.45, 16.86) * mm});
            skLineSegment(sketch, "E699", {"start": v(-82.45, 16.86) * mm, "end": v(-82.45, 17.09) * mm});
            skLineSegment(sketch, "E700", {"start": v(-82.45, 17.09) * mm, "end": v(-82.64, 17.78) * mm});
            skLineSegment(sketch, "E701", {"start": v(-82.64, 17.78) * mm, "end": v(-83.03, 18.35) * mm});
            skLineSegment(sketch, "E702", {"start": v(-83.03, 18.35) * mm, "end": v(-83.13, 18.44) * mm});
            skLineSegment(sketch, "E703", {"start": v(-83.13, 18.44) * mm, "end": v(-83.22, 18.5) * mm});
            skLineSegment(sketch, "E704", {"start": v(-83.22, 18.5) * mm, "end": v(-83.72, 18.75) * mm});
            skLineSegment(sketch, "E705", {"start": v(-83.72, 18.75) * mm, "end": v(-84.27, 18.86) * mm});
            skLineSegment(sketch, "E706", {"start": v(-84.27, 18.86) * mm, "end": v(-84.45, 18.86) * mm});
            skLineSegment(sketch, "E707", {"start": v(-84.45, 18.86) * mm, "end": v(-84.64, 18.86) * mm});
            skLineSegment(sketch, "E708", {"start": v(-84.64, 18.86) * mm, "end": v(-85.19, 18.75) * mm});
            skLineSegment(sketch, "E709", {"start": v(-85.19, 18.75) * mm, "end": v(-85.7, 18.5) * mm});
            skLineSegment(sketch, "E710", {"start": v(-85.7, 18.5) * mm, "end": v(-85.78, 18.44) * mm});
            skLineSegment(sketch, "E711", {"start": v(-85.78, 18.44) * mm, "end": v(-85.88, 18.35) * mm});
            skLineSegment(sketch, "E712", {"start": v(-85.88, 18.35) * mm, "end": v(-86.27, 17.78) * mm});
            skLineSegment(sketch, "E713", {"start": v(-86.27, 17.78) * mm, "end": v(-86.46, 17.09) * mm});
            skLineSegment(sketch, "E714", {"start": v(-86.46, 17.09) * mm, "end": v(-86.46, 16.86) * mm});
            skLineSegment(sketch, "E715", {"start": v(-86.46, 16.86) * mm, "end": v(-86.46, 16.62) * mm});
            skLineSegment(sketch, "E716", {"start": v(-86.46, 16.62) * mm, "end": v(-86.27, 15.92) * mm});
            skLineSegment(sketch, "E717", {"start": v(-86.27, 15.92) * mm, "end": v(-85.88, 15.36) * mm});
            skLineSegment(sketch, "E718", {"start": v(-85.88, 15.36) * mm, "end": v(-85.78, 15.28) * mm});
            skLineSegment(sketch, "E719", {"start": v(-85.78, 15.28) * mm, "end": v(-85.7, 15.2) * mm});
            skLineSegment(sketch, "E720", {"start": v(-85.7, 15.2) * mm, "end": v(-85.18, 14.94) * mm});
            skLineSegment(sketch, "E721", {"start": v(-85.18, 14.94) * mm, "end": v(-84.64, 14.83) * mm});
            skLineSegment(sketch, "E722", {"start": v(-84.64, 14.83) * mm, "end": v(-84.45, 14.83) * mm});
            skLineSegment(sketch, "E723", {"start": v(-78.9, 15.92) * mm, "end": v(-78.96, 15.85) * mm});
            skLineSegment(sketch, "E724", {"start": v(-78.96, 15.85) * mm, "end": v(-79.38, 15.63) * mm});
            skLineSegment(sketch, "E725", {"start": v(-79.38, 15.63) * mm, "end": v(-79.89, 15.56) * mm});
            skLineSegment(sketch, "E726", {"start": v(-79.89, 15.56) * mm, "end": v(-80.06, 15.56) * mm});
            skLineSegment(sketch, "E727", {"start": v(-80.06, 15.56) * mm, "end": v(-80.8, 15.56) * mm});
            skLineSegment(sketch, "E728", {"start": v(-80.8, 15.56) * mm, "end": v(-80.8, 17.92) * mm});
            skLineSegment(sketch, "E729", {"start": v(-80.8, 17.92) * mm, "end": v(-80.8, 18.05) * mm});
            skLineSegment(sketch, "E730", {"start": v(-80.8, 18.05) * mm, "end": v(-80.73, 18.42) * mm});
            skLineSegment(sketch, "E731", {"start": v(-80.73, 18.42) * mm, "end": v(-80.57, 18.75) * mm});
            skLineSegment(sketch, "E732", {"start": v(-80.57, 18.75) * mm, "end": v(-80.53, 18.78) * mm});
            skLineSegment(sketch, "E733", {"start": v(-80.53, 18.78) * mm, "end": v(-81.92, 18.78) * mm});
            skLineSegment(sketch, "E734", {"start": v(-81.92, 18.78) * mm, "end": v(-81.87, 18.75) * mm});
            skLineSegment(sketch, "E735", {"start": v(-81.87, 18.75) * mm, "end": v(-81.7, 18.42) * mm});
            skLineSegment(sketch, "E736", {"start": v(-81.7, 18.42) * mm, "end": v(-81.62, 18.05) * mm});
            skLineSegment(sketch, "E737", {"start": v(-81.62, 18.05) * mm, "end": v(-81.62, 17.92) * mm});
            skLineSegment(sketch, "E738", {"start": v(-81.62, 17.92) * mm, "end": v(-81.62, 15.77) * mm});
            skLineSegment(sketch, "E739", {"start": v(-81.62, 15.77) * mm, "end": v(-81.62, 15.64) * mm});
            skLineSegment(sketch, "E740", {"start": v(-81.62, 15.64) * mm, "end": v(-81.7, 15.27) * mm});
            skLineSegment(sketch, "E741", {"start": v(-81.7, 15.27) * mm, "end": v(-81.87, 14.97) * mm});
            skLineSegment(sketch, "E742", {"start": v(-81.87, 14.97) * mm, "end": v(-81.92, 14.94) * mm});
            skLineSegment(sketch, "E743", {"start": v(-81.92, 14.94) * mm, "end": v(-79.03, 14.94) * mm});
            skLineSegment(sketch, "E744", {"start": v(-79.03, 14.94) * mm, "end": v(-78.9, 15.92) * mm});
            skLineSegment(sketch, "E745", {"start": v(-75.43, 15.92) * mm, "end": v(-75.48, 15.85) * mm});
            skLineSegment(sketch, "E746", {"start": v(-75.48, 15.85) * mm, "end": v(-75.9, 15.63) * mm});
            skLineSegment(sketch, "E747", {"start": v(-75.9, 15.63) * mm, "end": v(-76.46, 15.55) * mm});
            skLineSegment(sketch, "E748", {"start": v(-76.46, 15.55) * mm, "end": v(-76.58, 15.56) * mm});
            skLineSegment(sketch, "E749", {"start": v(-76.58, 15.56) * mm, "end": v(-77.35, 15.56) * mm});
            skLineSegment(sketch, "E750", {"start": v(-77.35, 15.56) * mm, "end": v(-77.35, 17.92) * mm});
            skLineSegment(sketch, "E751", {"start": v(-77.35, 17.92) * mm, "end": v(-77.35, 18.05) * mm});
            skLineSegment(sketch, "E752", {"start": v(-77.35, 18.05) * mm, "end": v(-77.27, 18.42) * mm});
            skLineSegment(sketch, "E753", {"start": v(-77.27, 18.42) * mm, "end": v(-77.1, 18.75) * mm});
            skLineSegment(sketch, "E754", {"start": v(-77.1, 18.75) * mm, "end": v(-77.05, 18.78) * mm});
            skLineSegment(sketch, "E755", {"start": v(-77.05, 18.78) * mm, "end": v(-78.44, 18.78) * mm});
            skLineSegment(sketch, "E756", {"start": v(-78.44, 18.78) * mm, "end": v(-78.39, 18.75) * mm});
            skLineSegment(sketch, "E757", {"start": v(-78.39, 18.75) * mm, "end": v(-78.22, 18.42) * mm});
            skLineSegment(sketch, "E758", {"start": v(-78.22, 18.42) * mm, "end": v(-78.14, 18.05) * mm});
            skLineSegment(sketch, "E759", {"start": v(-78.14, 18.05) * mm, "end": v(-78.14, 17.92) * mm});
            skLineSegment(sketch, "E760", {"start": v(-78.14, 17.92) * mm, "end": v(-78.14, 15.77) * mm});
            skLineSegment(sketch, "E761", {"start": v(-78.14, 15.77) * mm, "end": v(-78.14, 15.64) * mm});
            skLineSegment(sketch, "E762", {"start": v(-78.14, 15.64) * mm, "end": v(-78.22, 15.26) * mm});
            skLineSegment(sketch, "E763", {"start": v(-78.22, 15.26) * mm, "end": v(-78.39, 14.95) * mm});
            skLineSegment(sketch, "E764", {"start": v(-78.39, 14.95) * mm, "end": v(-78.44, 14.91) * mm});
            skLineSegment(sketch, "E765", {"start": v(-78.44, 14.91) * mm, "end": v(-75.58, 14.91) * mm});
            skLineSegment(sketch, "E766", {"start": v(-75.58, 14.91) * mm, "end": v(-75.43, 15.92) * mm});
            skLineSegment(sketch, "E767", {"start": v(-67.7, 18.27) * mm, "end": v(-67.7, 18.64) * mm});
            skLineSegment(sketch, "E768", {"start": v(-67.7, 18.64) * mm, "end": v(-68, 19.75) * mm});
            skLineSegment(sketch, "E769", {"start": v(-68, 19.75) * mm, "end": v(-68.82, 20.97) * mm});
            skLineSegment(sketch, "E770", {"start": v(-68.82, 20.97) * mm, "end": v(-70.04, 21.79) * mm});
            skLineSegment(sketch, "E771", {"start": v(-70.04, 21.79) * mm, "end": v(-71.15, 22.08) * mm});
            skLineSegment(sketch, "E772", {"start": v(-71.15, 22.08) * mm, "end": v(-71.52, 22.08) * mm});
            skLineSegment(sketch, "E773", {"start": v(-71.52, 22.08) * mm, "end": v(-90.92, 22.08) * mm});
            skLineSegment(sketch, "E774", {"start": v(-90.92, 22.08) * mm, "end": v(-91.3, 22.08) * mm});
            skLineSegment(sketch, "E775", {"start": v(-91.3, 22.08) * mm, "end": v(-92.4, 21.79) * mm});
            skLineSegment(sketch, "E776", {"start": v(-92.4, 21.79) * mm, "end": v(-93.62, 20.97) * mm});
            skLineSegment(sketch, "E777", {"start": v(-93.62, 20.97) * mm, "end": v(-94.44, 19.75) * mm});
            skLineSegment(sketch, "E778", {"start": v(-94.44, 19.75) * mm, "end": v(-94.74, 18.64) * mm});
            skLineSegment(sketch, "E779", {"start": v(-94.74, 18.64) * mm, "end": v(-94.74, 18.27) * mm});
            skLineSegment(sketch, "E780", {"start": v(-94.74, 18.27) * mm, "end": v(-94.74, -18.26) * mm});
            skLineSegment(sketch, "E781", {"start": v(-94.74, -18.26) * mm, "end": v(-94.74, -18.64) * mm});
            skLineSegment(sketch, "E782", {"start": v(-94.74, -18.64) * mm, "end": v(-94.44, -19.75) * mm});
            skLineSegment(sketch, "E783", {"start": v(-94.44, -19.75) * mm, "end": v(-93.62, -20.97) * mm});
            skLineSegment(sketch, "E784", {"start": v(-93.62, -20.97) * mm, "end": v(-92.4, -21.78) * mm});
            skLineSegment(sketch, "E785", {"start": v(-92.4, -21.78) * mm, "end": v(-91.3, -22.08) * mm});
            skLineSegment(sketch, "E786", {"start": v(-91.3, -22.08) * mm, "end": v(-90.92, -22.08) * mm});
            skLineSegment(sketch, "E787", {"start": v(-90.92, -22.08) * mm, "end": v(-71.52, -22.08) * mm});
            skLineSegment(sketch, "E788", {"start": v(-71.52, -22.08) * mm, "end": v(-71.15, -22.08) * mm});
            skLineSegment(sketch, "E789", {"start": v(-71.15, -22.08) * mm, "end": v(-70.04, -21.78) * mm});
            skLineSegment(sketch, "E790", {"start": v(-70.04, -21.78) * mm, "end": v(-68.82, -20.97) * mm});
            skLineSegment(sketch, "E791", {"start": v(-68.82, -20.97) * mm, "end": v(-68, -19.75) * mm});
            skLineSegment(sketch, "E792", {"start": v(-68, -19.75) * mm, "end": v(-67.7, -18.64) * mm});
            skLineSegment(sketch, "E793", {"start": v(-67.7, -18.64) * mm, "end": v(-67.7, -18.26) * mm});
            skLineSegment(sketch, "E794", {"start": v(-67.7, -18.26) * mm, "end": v(-67.7, 18.27) * mm});
            skLineSegment(sketch, "E795", {"start": v(-92.4, -13.96) * mm, "end": v(-92.4, -18.26) * mm});
            skLineSegment(sketch, "E796", {"start": v(-92.4, -18.26) * mm, "end": v(-92.4, -18.4) * mm});
            skLineSegment(sketch, "E797", {"start": v(-92.4, -18.4) * mm, "end": v(-92.28, -18.84) * mm});
            skLineSegment(sketch, "E798", {"start": v(-92.28, -18.84) * mm, "end": v(-91.96, -19.3) * mm});
            skLineSegment(sketch, "E799", {"start": v(-91.96, -19.3) * mm, "end": v(-91.5, -19.62) * mm});
            skLineSegment(sketch, "E800", {"start": v(-91.5, -19.62) * mm, "end": v(-91.06, -19.74) * mm});
            skLineSegment(sketch, "E801", {"start": v(-91.06, -19.74) * mm, "end": v(-90.92, -19.74) * mm});
            skLineSegment(sketch, "E802", {"start": v(-90.92, -19.74) * mm, "end": v(-71.52, -19.74) * mm});
            skLineSegment(sketch, "E803", {"start": v(-71.52, -19.74) * mm, "end": v(-71.38, -19.74) * mm});
            skLineSegment(sketch, "E804", {"start": v(-71.38, -19.74) * mm, "end": v(-70.94, -19.62) * mm});
            skLineSegment(sketch, "E805", {"start": v(-70.94, -19.62) * mm, "end": v(-70.47, -19.3) * mm});
            skLineSegment(sketch, "E806", {"start": v(-70.47, -19.3) * mm, "end": v(-70.15, -18.84) * mm});
            skLineSegment(sketch, "E807", {"start": v(-70.15, -18.84) * mm, "end": v(-70.03, -18.4) * mm});
            skLineSegment(sketch, "E808", {"start": v(-70.03, -18.4) * mm, "end": v(-70.03, -18.26) * mm});
            skLineSegment(sketch, "E809", {"start": v(-70.03, -18.26) * mm, "end": v(-70.03, -13.96) * mm});
            skLineSegment(sketch, "E810", {"start": v(-70.03, -13.96) * mm, "end": v(-92.4, -13.96) * mm});
            skLineSegment(sketch, "E811", {"start": v(-82.8, -8.8) * mm, "end": v(-82.8, -3.05) * mm});
            skLineSegment(sketch, "E812", {"start": v(-82.8, -3.05) * mm, "end": v(-82.67, -3.05) * mm});
            skLineSegment(sketch, "E813", {"start": v(-82.67, -3.05) * mm, "end": v(-81.32, -2.98) * mm});
            skLineSegment(sketch, "E814", {"start": v(-81.32, -2.98) * mm, "end": v(-81.19, -2.96) * mm});
            skLineSegment(sketch, "E815", {"start": v(-81.19, -2.96) * mm, "end": v(-81.24, -2.85) * mm});
            skLineSegment(sketch, "E816", {"start": v(-81.24, -2.85) * mm, "end": v(-81.75, -1.75) * mm});
            skLineSegment(sketch, "E817", {"start": v(-81.75, -1.75) * mm, "end": v(-81.8, -1.64) * mm});
            skLineSegment(sketch, "E818", {"start": v(-81.8, -1.64) * mm, "end": v(-81.89, -1.65) * mm});
            skLineSegment(sketch, "E819", {"start": v(-81.89, -1.65) * mm, "end": v(-82.73, -1.7) * mm});
            skLineSegment(sketch, "E820", {"start": v(-82.73, -1.7) * mm, "end": v(-82.8, -1.7) * mm});
            skLineSegment(sketch, "E821", {"start": v(-82.8, -1.7) * mm, "end": v(-82.8, -0.51) * mm});
            skLineSegment(sketch, "E822", {"start": v(-82.8, -0.51) * mm, "end": v(-83, -0.56) * mm});
            skLineSegment(sketch, "E823", {"start": v(-83, -0.56) * mm, "end": v(-85, -0.87) * mm});
            skLineSegment(sketch, "E824", {"start": v(-85, -0.87) * mm, "end": v(-85.2, -0.9) * mm});
            skLineSegment(sketch, "E825", {"start": v(-85.2, -0.9) * mm, "end": v(-85.2, -8.8) * mm});
            skLineSegment(sketch, "E826", {"start": v(-85.2, -8.8) * mm, "end": v(-85.2, -9.06) * mm});
            skLineSegment(sketch, "E827", {"start": v(-85.2, -9.06) * mm, "end": v(-85.33, -9.88) * mm});
            skLineSegment(sketch, "E828", {"start": v(-85.33, -9.88) * mm, "end": v(-85.67, -10.6) * mm});
            skLineSegment(sketch, "E829", {"start": v(-85.67, -10.6) * mm, "end": v(-86.1, -11.04) * mm});
            skLineSegment(sketch, "E830", {"start": v(-86.1, -11.04) * mm, "end": v(-86.4, -11.26) * mm});
            skLineSegment(sketch, "E831", {"start": v(-86.4, -11.26) * mm, "end": v(-86.5, -11.33) * mm});
            skLineSegment(sketch, "E832", {"start": v(-86.5, -11.33) * mm, "end": v(-81.5, -11.33) * mm});
            skLineSegment(sketch, "E833", {"start": v(-81.5, -11.33) * mm, "end": v(-81.61, -11.26) * mm});
            skLineSegment(sketch, "E834", {"start": v(-81.61, -11.26) * mm, "end": v(-81.91, -11.04) * mm});
            skLineSegment(sketch, "E835", {"start": v(-81.91, -11.04) * mm, "end": v(-82.34, -10.6) * mm});
            skLineSegment(sketch, "E836", {"start": v(-82.34, -10.6) * mm, "end": v(-82.67, -9.88) * mm});
            skLineSegment(sketch, "E837", {"start": v(-82.67, -9.88) * mm, "end": v(-82.8, -9.06) * mm});
            skLineSegment(sketch, "E838", {"start": v(-82.8, -9.06) * mm, "end": v(-82.8, -8.8) * mm});
            skLineSegment(sketch, "E839", {"start": v(-71.2, -11.3) * mm, "end": v(-71.3, -11.21) * mm});
            skLineSegment(sketch, "E840", {"start": v(-71.3, -11.21) * mm, "end": v(-71.85, -10.53) * mm});
            skLineSegment(sketch, "E841", {"start": v(-71.85, -10.53) * mm, "end": v(-72.31, -9.45) * mm});
            skLineSegment(sketch, "E842", {"start": v(-72.31, -9.45) * mm, "end": v(-72.38, -9.15) * mm});
            skLineSegment(sketch, "E843", {"start": v(-72.38, -9.15) * mm, "end": v(-72.47, -8.7) * mm});
            skLineSegment(sketch, "E844", {"start": v(-72.47, -8.7) * mm, "end": v(-72.83, -7.39) * mm});
            skLineSegment(sketch, "E845", {"start": v(-72.83, -7.39) * mm, "end": v(-73.54, -5.43) * mm});
            skLineSegment(sketch, "E846", {"start": v(-73.54, -5.43) * mm, "end": v(-74.54, -3.45) * mm});
            skLineSegment(sketch, "E847", {"start": v(-74.54, -3.45) * mm, "end": v(-75.52, -2.02) * mm});
            skLineSegment(sketch, "E848", {"start": v(-75.52, -2.02) * mm, "end": v(-75.9, -1.6) * mm});
            skLineSegment(sketch, "E849", {"start": v(-75.9, -1.6) * mm, "end": v(-75.54, -1.4) * mm});
            skLineSegment(sketch, "E850", {"start": v(-75.54, -1.4) * mm, "end": v(-74.53, -0.65) * mm});
            skLineSegment(sketch, "E851", {"start": v(-74.53, -0.65) * mm, "end": v(-73.5, 0.52) * mm});
            skLineSegment(sketch, "E852", {"start": v(-73.5, 0.52) * mm, "end": v(-72.86, 1.88) * mm});
            skLineSegment(sketch, "E853", {"start": v(-72.86, 1.88) * mm, "end": v(-72.63, 3.03) * mm});
            skLineSegment(sketch, "E854", {"start": v(-72.63, 3.03) * mm, "end": v(-72.63, 3.41) * mm});
            skLineSegment(sketch, "E855", {"start": v(-72.63, 3.41) * mm, "end": v(-72.63, 3.7) * mm});
            skLineSegment(sketch, "E856", {"start": v(-72.63, 3.7) * mm, "end": v(-72.77, 4.57) * mm});
            skLineSegment(sketch, "E857", {"start": v(-72.77, 4.57) * mm, "end": v(-73.19, 5.69) * mm});
            skLineSegment(sketch, "E858", {"start": v(-73.19, 5.69) * mm, "end": v(-73.87, 6.7) * mm});
            skLineSegment(sketch, "E859", {"start": v(-73.87, 6.7) * mm, "end": v(-74.55, 7.36) * mm});
            skLineSegment(sketch, "E860", {"start": v(-74.55, 7.36) * mm, "end": v(-74.8, 7.53) * mm});
            skLineSegment(sketch, "E861", {"start": v(-74.8, 7.53) * mm, "end": v(-74.96, 7.63) * mm});
            skLineSegment(sketch, "E862", {"start": v(-74.96, 7.63) * mm, "end": v(-75.79, 8.03) * mm});
            skLineSegment(sketch, "E863", {"start": v(-75.79, 8.03) * mm, "end": v(-76.74, 8.32) * mm});
            skLineSegment(sketch, "E864", {"start": v(-76.74, 8.32) * mm, "end": v(-76.94, 8.36) * mm});
            skLineSegment(sketch, "E865", {"start": v(-76.94, 8.36) * mm, "end": v(-76.87, 8.2) * mm});
            skLineSegment(sketch, "E866", {"start": v(-76.87, 8.2) * mm, "end": v(-76.42, 6.53) * mm});
            skLineSegment(sketch, "E867", {"start": v(-76.42, 6.53) * mm, "end": v(-76.4, 6.36) * mm});
            skLineSegment(sketch, "E868", {"start": v(-76.4, 6.36) * mm, "end": v(-76.2, 6.19) * mm});
            skLineSegment(sketch, "E869", {"start": v(-76.2, 6.19) * mm, "end": v(-75.4, 5.08) * mm});
            skLineSegment(sketch, "E870", {"start": v(-75.4, 5.08) * mm, "end": v(-75.07, 3.8) * mm});
            skLineSegment(sketch, "E871", {"start": v(-75.07, 3.8) * mm, "end": v(-75.07, 3.37) * mm});
            skLineSegment(sketch, "E872", {"start": v(-75.07, 3.37) * mm, "end": v(-75.07, 3.06) * mm});
            skLineSegment(sketch, "E873", {"start": v(-75.07, 3.06) * mm, "end": v(-75.24, 2.14) * mm});
            skLineSegment(sketch, "E874", {"start": v(-75.24, 2.14) * mm, "end": v(-75.83, 0.91) * mm});
            skLineSegment(sketch, "E875", {"start": v(-75.83, 0.91) * mm, "end": v(-76.95, -0.2) * mm});
            skLineSegment(sketch, "E876", {"start": v(-76.95, -0.2) * mm, "end": v(-78.25, -0.9) * mm});
            skLineSegment(sketch, "E877", {"start": v(-78.25, -0.9) * mm, "end": v(-78.71, -1.07) * mm});
            skLineSegment(sketch, "E878", {"start": v(-78.71, -1.07) * mm, "end": v(-78.66, -1.18) * mm});
            skLineSegment(sketch, "E879", {"start": v(-78.66, -1.18) * mm, "end": v(-78.1, -2.32) * mm});
            skLineSegment(sketch, "E880", {"start": v(-78.1, -2.32) * mm, "end": v(-78.05, -2.43) * mm});
            skLineSegment(sketch, "E881", {"start": v(-78.05, -2.43) * mm, "end": v(-78.01, -2.42) * mm});
            skLineSegment(sketch, "E882", {"start": v(-78.01, -2.42) * mm, "end": v(-77.64, -2.32) * mm});
            skLineSegment(sketch, "E883", {"start": v(-77.64, -2.32) * mm, "end": v(-77.6, -2.3) * mm});
            skLineSegment(sketch, "E884", {"start": v(-77.6, -2.3) * mm, "end": v(-77.27, -2.69) * mm});
            skLineSegment(sketch, "E885", {"start": v(-77.27, -2.69) * mm, "end": v(-75.87, -5.13) * mm});
            skLineSegment(sketch, "E886", {"start": v(-75.87, -5.13) * mm, "end": v(-74.97, -7.93) * mm});
            skLineSegment(sketch, "E887", {"start": v(-74.97, -7.93) * mm, "end": v(-74.9, -8.5) * mm});
            skLineSegment(sketch, "E888", {"start": v(-74.9, -8.5) * mm, "end": v(-74.86, -8.75) * mm});
            skLineSegment(sketch, "E889", {"start": v(-74.86, -8.75) * mm, "end": v(-74.86, -9.56) * mm});
            skLineSegment(sketch, "E890", {"start": v(-74.86, -9.56) * mm, "end": v(-75.03, -10.36) * mm});
            skLineSegment(sketch, "E891", {"start": v(-75.03, -10.36) * mm, "end": v(-75.31, -10.93) * mm});
            skLineSegment(sketch, "E892", {"start": v(-75.31, -10.93) * mm, "end": v(-75.54, -11.22) * mm});
            skLineSegment(sketch, "E893", {"start": v(-75.54, -11.22) * mm, "end": v(-75.62, -11.3) * mm});
            skLineSegment(sketch, "E894", {"start": v(-75.62, -11.3) * mm, "end": v(-71.2, -11.3) * mm});
            skLineSegment(sketch, "E895", {"start": v(-76.17, -8.73) * mm, "end": v(-76.28, -8.63) * mm});
            skLineSegment(sketch, "E896", {"start": v(-76.28, -8.63) * mm, "end": v(-76.83, -7.94) * mm});
            skLineSegment(sketch, "E897", {"start": v(-76.83, -7.94) * mm, "end": v(-77.29, -6.86) * mm});
            skLineSegment(sketch, "E898", {"start": v(-77.29, -6.86) * mm, "end": v(-77.35, -6.57) * mm});
            skLineSegment(sketch, "E899", {"start": v(-77.35, -6.57) * mm, "end": v(-77.47, -6.03) * mm});
            skLineSegment(sketch, "E900", {"start": v(-77.47, -6.03) * mm, "end": v(-78.46, -2.9) * mm});
            skLineSegment(sketch, "E901", {"start": v(-78.46, -2.9) * mm, "end": v(-80.17, 0.23) * mm});
            skLineSegment(sketch, "E902", {"start": v(-80.17, 0.23) * mm, "end": v(-80.63, 0.77) * mm});
            skLineSegment(sketch, "E903", {"start": v(-80.63, 0.77) * mm, "end": v(-80.61, 0.78) * mm});
            skLineSegment(sketch, "E904", {"start": v(-80.61, 0.78) * mm, "end": v(-80.42, 0.87) * mm});
            skLineSegment(sketch, "E905", {"start": v(-80.42, 0.87) * mm, "end": v(-80.4, 0.88) * mm});
            skLineSegment(sketch, "E906", {"start": v(-80.4, 0.88) * mm, "end": v(-80.02, 1.07) * mm});
            skLineSegment(sketch, "E907", {"start": v(-80.02, 1.07) * mm, "end": v(-78.96, 1.82) * mm});
            skLineSegment(sketch, "E908", {"start": v(-78.96, 1.82) * mm, "end": v(-77.88, 3.01) * mm});
            skLineSegment(sketch, "E909", {"start": v(-77.88, 3.01) * mm, "end": v(-77.2, 4.41) * mm});
            skLineSegment(sketch, "E910", {"start": v(-77.2, 4.41) * mm, "end": v(-76.96, 5.6) * mm});
            skLineSegment(sketch, "E911", {"start": v(-76.96, 5.6) * mm, "end": v(-76.96, 6) * mm});
            skLineSegment(sketch, "E912", {"start": v(-76.96, 6) * mm, "end": v(-76.96, 6.29) * mm});
            skLineSegment(sketch, "E913", {"start": v(-76.96, 6.29) * mm, "end": v(-77.1, 7.16) * mm});
            skLineSegment(sketch, "E914", {"start": v(-77.1, 7.16) * mm, "end": v(-77.52, 8.28) * mm});
            skLineSegment(sketch, "E915", {"start": v(-77.52, 8.28) * mm, "end": v(-78.2, 9.29) * mm});
            skLineSegment(sketch, "E916", {"start": v(-78.2, 9.29) * mm, "end": v(-78.89, 9.94) * mm});
            skLineSegment(sketch, "E917", {"start": v(-78.89, 9.94) * mm, "end": v(-79.14, 10.11) * mm});
            skLineSegment(sketch, "E918", {"start": v(-79.14, 10.11) * mm, "end": v(-79.42, 10.3) * mm});
            skLineSegment(sketch, "E919", {"start": v(-79.42, 10.3) * mm, "end": v(-81.1, 10.92) * mm});
            skLineSegment(sketch, "E920", {"start": v(-81.1, 10.92) * mm, "end": v(-83, 11.16) * mm});
            skLineSegment(sketch, "E921", {"start": v(-83, 11.16) * mm, "end": v(-83.64, 11.16) * mm});
            skLineSegment(sketch, "E922", {"start": v(-83.64, 11.16) * mm, "end": v(-90.83, 11.16) * mm});
            skLineSegment(sketch, "E923", {"start": v(-90.83, 11.16) * mm, "end": v(-90.73, 11.1) * mm});
            skLineSegment(sketch, "E924", {"start": v(-90.73, 11.1) * mm, "end": v(-90.42, 10.87) * mm});
            skLineSegment(sketch, "E925", {"start": v(-90.42, 10.87) * mm, "end": v(-90, 10.43) * mm});
            skLineSegment(sketch, "E926", {"start": v(-90, 10.43) * mm, "end": v(-89.67, 9.71) * mm});
            skLineSegment(sketch, "E927", {"start": v(-89.67, 9.71) * mm, "end": v(-89.53, 8.9) * mm});
            skLineSegment(sketch, "E928", {"start": v(-89.53, 8.9) * mm, "end": v(-89.53, 8.62) * mm});
            skLineSegment(sketch, "E929", {"start": v(-89.53, 8.62) * mm, "end": v(-89.53, -6.19) * mm});
            skLineSegment(sketch, "E930", {"start": v(-89.53, -6.19) * mm, "end": v(-89.53, -6.46) * mm});
            skLineSegment(sketch, "E931", {"start": v(-89.53, -6.46) * mm, "end": v(-89.67, -7.29) * mm});
            skLineSegment(sketch, "E932", {"start": v(-89.67, -7.29) * mm, "end": v(-90, -8) * mm});
            skLineSegment(sketch, "E933", {"start": v(-90, -8) * mm, "end": v(-90.42, -8.44) * mm});
            skLineSegment(sketch, "E934", {"start": v(-90.42, -8.44) * mm, "end": v(-90.73, -8.66) * mm});
            skLineSegment(sketch, "E935", {"start": v(-90.73, -8.66) * mm, "end": v(-90.83, -8.73) * mm});
            skLineSegment(sketch, "E936", {"start": v(-90.83, -8.73) * mm, "end": v(-85.84, -8.73) * mm});
            skLineSegment(sketch, "E937", {"start": v(-85.84, -8.73) * mm, "end": v(-85.94, -8.66) * mm});
            skLineSegment(sketch, "E938", {"start": v(-85.94, -8.66) * mm, "end": v(-86.24, -8.44) * mm});
            skLineSegment(sketch, "E939", {"start": v(-86.24, -8.44) * mm, "end": v(-86.67, -8) * mm});
            skLineSegment(sketch, "E940", {"start": v(-86.67, -8) * mm, "end": v(-87, -7.29) * mm});
            skLineSegment(sketch, "E941", {"start": v(-87, -7.29) * mm, "end": v(-87.14, -6.46) * mm});
            skLineSegment(sketch, "E942", {"start": v(-87.14, -6.46) * mm, "end": v(-87.14, -6.19) * mm});
            skLineSegment(sketch, "E943", {"start": v(-87.14, -6.19) * mm, "end": v(-87.14, -0.45) * mm});
            skLineSegment(sketch, "E944", {"start": v(-87.14, -0.45) * mm, "end": v(-86.51, -0.45) * mm});
            skLineSegment(sketch, "E945", {"start": v(-86.51, -0.45) * mm, "end": v(-84.62, -0.3) * mm});
            skLineSegment(sketch, "E946", {"start": v(-84.62, -0.3) * mm, "end": v(-82.71, 0.04) * mm});
            skLineSegment(sketch, "E947", {"start": v(-82.71, 0.04) * mm, "end": v(-82.36, 0.13) * mm});
            skLineSegment(sketch, "E948", {"start": v(-82.36, 0.13) * mm, "end": v(-82.05, -0.25) * mm});
            skLineSegment(sketch, "E949", {"start": v(-82.05, -0.25) * mm, "end": v(-80.76, -2.64) * mm});
            skLineSegment(sketch, "E950", {"start": v(-80.76, -2.64) * mm, "end": v(-79.94, -5.35) * mm});
            skLineSegment(sketch, "E951", {"start": v(-79.94, -5.35) * mm, "end": v(-79.87, -5.89) * mm});
            skLineSegment(sketch, "E952", {"start": v(-79.87, -5.89) * mm, "end": v(-79.83, -6.15) * mm});
            skLineSegment(sketch, "E953", {"start": v(-79.83, -6.15) * mm, "end": v(-79.84, -6.96) * mm});
            skLineSegment(sketch, "E954", {"start": v(-79.84, -6.96) * mm, "end": v(-80, -7.77) * mm});
            skLineSegment(sketch, "E955", {"start": v(-80, -7.77) * mm, "end": v(-80.29, -8.35) * mm});
            skLineSegment(sketch, "E956", {"start": v(-80.29, -8.35) * mm, "end": v(-80.5, -8.64) * mm});
            skLineSegment(sketch, "E957", {"start": v(-80.5, -8.64) * mm, "end": v(-80.6, -8.73) * mm});
            skLineSegment(sketch, "E958", {"start": v(-80.6, -8.73) * mm, "end": v(-76.17, -8.73) * mm});
            skLineSegment(sketch, "E959", {"start": v(-87.14, 0.88) * mm, "end": v(-87.14, 9.84) * mm});
            skLineSegment(sketch, "E960", {"start": v(-87.14, 9.84) * mm, "end": v(-83.75, 9.84) * mm});
            skLineSegment(sketch, "E961", {"start": v(-83.75, 9.84) * mm, "end": v(-83.44, 9.83) * mm});
            skLineSegment(sketch, "E962", {"start": v(-83.44, 9.83) * mm, "end": v(-82.12, 9.63) * mm});
            skLineSegment(sketch, "E963", {"start": v(-82.12, 9.63) * mm, "end": v(-81.05, 9.18) * mm});
            skLineSegment(sketch, "E964", {"start": v(-81.05, 9.18) * mm, "end": v(-80.87, 9.05) * mm});
            skLineSegment(sketch, "E965", {"start": v(-80.87, 9.05) * mm, "end": v(-80.63, 8.88) * mm});
            skLineSegment(sketch, "E966", {"start": v(-80.63, 8.88) * mm, "end": v(-79.77, 7.74) * mm});
            skLineSegment(sketch, "E967", {"start": v(-79.77, 7.74) * mm, "end": v(-79.4, 6.42) * mm});
            skLineSegment(sketch, "E968", {"start": v(-79.4, 6.42) * mm, "end": v(-79.4, 5.98) * mm});
            skLineSegment(sketch, "E969", {"start": v(-79.4, 5.98) * mm, "end": v(-79.4, 5.55) * mm});
            skLineSegment(sketch, "E970", {"start": v(-79.4, 5.55) * mm, "end": v(-79.73, 4.27) * mm});
            skLineSegment(sketch, "E971", {"start": v(-79.73, 4.27) * mm, "end": v(-80.93, 2.64) * mm});
            skLineSegment(sketch, "E972", {"start": v(-80.93, 2.64) * mm, "end": v(-83.3, 1.4) * mm});
            skLineSegment(sketch, "E973", {"start": v(-83.3, 1.4) * mm, "end": v(-86.18, 0.9) * mm});
            skLineSegment(sketch, "E974", {"start": v(-86.18, 0.9) * mm, "end": v(-87.14, 0.88) * mm});
            skLineSegment(sketch, "E975", {"start": v(-82.8, 2.16) * mm, "end": v(-82.8, 7.21) * mm});
            skLineSegment(sketch, "E976", {"start": v(-82.8, 7.21) * mm, "end": v(-80.12, 7.21) * mm});
            skLineSegment(sketch, "E977", {"start": v(-80.12, 7.21) * mm, "end": v(-80.17, 7.35) * mm});
            skLineSegment(sketch, "E978", {"start": v(-80.17, 7.35) * mm, "end": v(-80.52, 7.97) * mm});
            skLineSegment(sketch, "E979", {"start": v(-80.52, 7.97) * mm, "end": v(-81, 8.47) * mm});
            skLineSegment(sketch, "E980", {"start": v(-81, 8.47) * mm, "end": v(-81.12, 8.56) * mm});
            skLineSegment(sketch, "E981", {"start": v(-81.12, 8.56) * mm, "end": v(-86.5, 8.56) * mm});
            skLineSegment(sketch, "E982", {"start": v(-86.5, 8.56) * mm, "end": v(-86.4, 8.5) * mm});
            skLineSegment(sketch, "E983", {"start": v(-86.4, 8.5) * mm, "end": v(-86.1, 8.28) * mm});
            skLineSegment(sketch, "E984", {"start": v(-86.1, 8.28) * mm, "end": v(-85.67, 7.83) * mm});
            skLineSegment(sketch, "E985", {"start": v(-85.67, 7.83) * mm, "end": v(-85.33, 7.12) * mm});
            skLineSegment(sketch, "E986", {"start": v(-85.33, 7.12) * mm, "end": v(-85.2, 6.3) * mm});
            skLineSegment(sketch, "E987", {"start": v(-85.2, 6.3) * mm, "end": v(-85.2, 6.02) * mm});
            skLineSegment(sketch, "E988", {"start": v(-85.2, 6.02) * mm, "end": v(-85.2, 1.56) * mm});
            skLineSegment(sketch, "E989", {"start": v(-85.2, 1.56) * mm, "end": v(-84.98, 1.6) * mm});
            skLineSegment(sketch, "E990", {"start": v(-84.98, 1.6) * mm, "end": v(-82.98, 2.09) * mm});
            skLineSegment(sketch, "E991", {"start": v(-82.98, 2.09) * mm, "end": v(-82.8, 2.16) * mm});
            skLineSegment(sketch, "E992", {"start": v(-77.93, -16.86) * mm, "end": v(-77.93, -16.98) * mm});
            skLineSegment(sketch, "E993", {"start": v(-77.93, -16.98) * mm, "end": v(-77.85, -17.36) * mm});
            skLineSegment(sketch, "E994", {"start": v(-77.85, -17.36) * mm, "end": v(-77.62, -17.77) * mm});
            skLineSegment(sketch, "E995", {"start": v(-77.62, -17.77) * mm, "end": v(-77.25, -18.04) * mm});
            skLineSegment(sketch, "E996", {"start": v(-77.25, -18.04) * mm, "end": v(-76.88, -18.14) * mm});
            skLineSegment(sketch, "E997", {"start": v(-76.88, -18.14) * mm, "end": v(-76.75, -18.14) * mm});
            skLineSegment(sketch, "E998", {"start": v(-76.75, -18.14) * mm, "end": v(-76.57, -18.14) * mm});
            skLineSegment(sketch, "E999", {"start": v(-76.57, -18.14) * mm, "end": v(-76.01, -18.03) * mm});
            skLineSegment(sketch, "E1000", {"start": v(-76.01, -18.03) * mm, "end": v(-75.57, -17.8) * mm});
            skLineSegment(sketch, "E1001", {"start": v(-75.57, -17.8) * mm, "end": v(-75.51, -17.73) * mm});
            skLineSegment(sketch, "E1002", {"start": v(-75.51, -17.73) * mm, "end": v(-75.64, -18.56) * mm});
            skLineSegment(sketch, "E1003", {"start": v(-75.64, -18.56) * mm, "end": v(-75.69, -18.58) * mm});
            skLineSegment(sketch, "E1004", {"start": v(-75.69, -18.58) * mm, "end": v(-76.05, -18.7) * mm});
            skLineSegment(sketch, "E1005", {"start": v(-76.05, -18.7) * mm, "end": v(-76.56, -18.76) * mm});
            skLineSegment(sketch, "E1006", {"start": v(-76.56, -18.76) * mm, "end": v(-76.73, -18.76) * mm});
            skLineSegment(sketch, "E1007", {"start": v(-76.73, -18.76) * mm, "end": v(-76.94, -18.76) * mm});
            skLineSegment(sketch, "E1008", {"start": v(-76.94, -18.76) * mm, "end": v(-77.55, -18.63) * mm});
            skLineSegment(sketch, "E1009", {"start": v(-77.55, -18.63) * mm, "end": v(-78.2, -18.25) * mm});
            skLineSegment(sketch, "E1010", {"start": v(-78.2, -18.25) * mm, "end": v(-78.6, -17.66) * mm});
            skLineSegment(sketch, "E1011", {"start": v(-78.6, -17.66) * mm, "end": v(-78.76, -17.06) * mm});
            skLineSegment(sketch, "E1012", {"start": v(-78.76, -17.06) * mm, "end": v(-78.76, -16.86) * mm});
            skLineSegment(sketch, "E1013", {"start": v(-78.76, -16.86) * mm, "end": v(-78.76, -16.64) * mm});
            skLineSegment(sketch, "E1014", {"start": v(-78.76, -16.64) * mm, "end": v(-78.58, -16.01) * mm});
            skLineSegment(sketch, "E1015", {"start": v(-78.58, -16.01) * mm, "end": v(-78.21, -15.48) * mm});
            skLineSegment(sketch, "E1016", {"start": v(-78.21, -15.48) * mm, "end": v(-78.12, -15.4) * mm});
            skLineSegment(sketch, "E1017", {"start": v(-78.12, -15.4) * mm, "end": v(-78.03, -15.33) * mm});
            skLineSegment(sketch, "E1018", {"start": v(-78.03, -15.33) * mm, "end": v(-77.51, -15.06) * mm});
            skLineSegment(sketch, "E1019", {"start": v(-77.51, -15.06) * mm, "end": v(-76.93, -14.94) * mm});
            skLineSegment(sketch, "E1020", {"start": v(-76.93, -14.94) * mm, "end": v(-76.73, -14.94) * mm});
            skLineSegment(sketch, "E1021", {"start": v(-76.73, -14.94) * mm, "end": v(-76.56, -14.94) * mm});
            skLineSegment(sketch, "E1022", {"start": v(-76.56, -14.94) * mm, "end": v(-76.05, -15) * mm});
            skLineSegment(sketch, "E1023", {"start": v(-76.05, -15) * mm, "end": v(-75.69, -15.12) * mm});
            skLineSegment(sketch, "E1024", {"start": v(-75.69, -15.12) * mm, "end": v(-75.64, -15.15) * mm});
            skLineSegment(sketch, "E1025", {"start": v(-75.64, -15.15) * mm, "end": v(-75.64, -15.94) * mm});
            skLineSegment(sketch, "E1026", {"start": v(-75.64, -15.94) * mm, "end": v(-75.7, -15.87) * mm});
            skLineSegment(sketch, "E1027", {"start": v(-75.7, -15.87) * mm, "end": v(-76.08, -15.65) * mm});
            skLineSegment(sketch, "E1028", {"start": v(-76.08, -15.65) * mm, "end": v(-76.59, -15.55) * mm});
            skLineSegment(sketch, "E1029", {"start": v(-76.59, -15.55) * mm, "end": v(-76.75, -15.55) * mm});
            skLineSegment(sketch, "E1030", {"start": v(-76.75, -15.55) * mm, "end": v(-76.88, -15.55) * mm});
            skLineSegment(sketch, "E1031", {"start": v(-76.88, -15.55) * mm, "end": v(-77.25, -15.65) * mm});
            skLineSegment(sketch, "E1032", {"start": v(-77.25, -15.65) * mm, "end": v(-77.62, -15.92) * mm});
            skLineSegment(sketch, "E1033", {"start": v(-77.62, -15.92) * mm, "end": v(-77.85, -16.34) * mm});
            skLineSegment(sketch, "E1034", {"start": v(-77.85, -16.34) * mm, "end": v(-77.93, -16.73) * mm});
            skLineSegment(sketch, "E1035", {"start": v(-77.93, -16.73) * mm, "end": v(-77.93, -16.86) * mm});
            skLineSegment(sketch, "E1036", {"start": v(-87.6, -17.75) * mm, "end": v(-87.63, -17.67) * mm});
            skLineSegment(sketch, "E1037", {"start": v(-87.63, -17.67) * mm, "end": v(-87.85, -17.3) * mm});
            skLineSegment(sketch, "E1038", {"start": v(-87.85, -17.3) * mm, "end": v(-88.1, -17.05) * mm});
            skLineSegment(sketch, "E1039", {"start": v(-88.1, -17.05) * mm, "end": v(-88.17, -17.03) * mm});
            skLineSegment(sketch, "E1040", {"start": v(-88.17, -17.03) * mm, "end": v(-88.03, -17) * mm});
            skLineSegment(sketch, "E1041", {"start": v(-88.03, -17) * mm, "end": v(-87.54, -16.7) * mm});
            skLineSegment(sketch, "E1042", {"start": v(-87.54, -16.7) * mm, "end": v(-87.32, -16.23) * mm});
            skLineSegment(sketch, "E1043", {"start": v(-87.32, -16.23) * mm, "end": v(-87.31, -16.1) * mm});
            skLineSegment(sketch, "E1044", {"start": v(-87.31, -16.1) * mm, "end": v(-87.31, -15.95) * mm});
            skLineSegment(sketch, "E1045", {"start": v(-87.31, -15.95) * mm, "end": v(-87.47, -15.48) * mm});
            skLineSegment(sketch, "E1046", {"start": v(-87.47, -15.48) * mm, "end": v(-87.81, -15.14) * mm});
            skLineSegment(sketch, "E1047", {"start": v(-87.81, -15.14) * mm, "end": v(-87.9, -15.1) * mm});
            skLineSegment(sketch, "E1048", {"start": v(-87.9, -15.1) * mm, "end": v(-87.97, -15.09) * mm});
            skLineSegment(sketch, "E1049", {"start": v(-87.97, -15.09) * mm, "end": v(-88.7, -15.02) * mm});
            skLineSegment(sketch, "E1050", {"start": v(-88.7, -15.02) * mm, "end": v(-88.93, -15.02) * mm});
            skLineSegment(sketch, "E1051", {"start": v(-88.93, -15.02) * mm, "end": v(-90.8, -15.02) * mm});
            skLineSegment(sketch, "E1052", {"start": v(-90.8, -15.02) * mm, "end": v(-90.75, -15.05) * mm});
            skLineSegment(sketch, "E1053", {"start": v(-90.75, -15.05) * mm, "end": v(-90.59, -15.34) * mm});
            skLineSegment(sketch, "E1054", {"start": v(-90.59, -15.34) * mm, "end": v(-90.51, -15.7) * mm});
            skLineSegment(sketch, "E1055", {"start": v(-90.51, -15.7) * mm, "end": v(-90.51, -15.83) * mm});
            skLineSegment(sketch, "E1056", {"start": v(-90.51, -15.83) * mm, "end": v(-90.51, -17.88) * mm});
            skLineSegment(sketch, "E1057", {"start": v(-90.51, -17.88) * mm, "end": v(-90.51, -18) * mm});
            skLineSegment(sketch, "E1058", {"start": v(-90.51, -18) * mm, "end": v(-90.59, -18.35) * mm});
            skLineSegment(sketch, "E1059", {"start": v(-90.59, -18.35) * mm, "end": v(-90.75, -18.66) * mm});
            skLineSegment(sketch, "E1060", {"start": v(-90.75, -18.66) * mm, "end": v(-90.8, -18.7) * mm});
            skLineSegment(sketch, "E1061", {"start": v(-90.8, -18.7) * mm, "end": v(-89.47, -18.7) * mm});
            skLineSegment(sketch, "E1062", {"start": v(-89.47, -18.7) * mm, "end": v(-89.51, -18.66) * mm});
            skLineSegment(sketch, "E1063", {"start": v(-89.51, -18.66) * mm, "end": v(-89.67, -18.35) * mm});
            skLineSegment(sketch, "E1064", {"start": v(-89.67, -18.35) * mm, "end": v(-89.75, -18) * mm});
            skLineSegment(sketch, "E1065", {"start": v(-89.75, -18) * mm, "end": v(-89.75, -17.88) * mm});
            skLineSegment(sketch, "E1066", {"start": v(-89.75, -17.88) * mm, "end": v(-89.75, -17.22) * mm});
            skLineSegment(sketch, "E1067", {"start": v(-89.75, -17.22) * mm, "end": v(-89.2, -17.22) * mm});
            skLineSegment(sketch, "E1068", {"start": v(-89.2, -17.22) * mm, "end": v(-89.1, -17.22) * mm});
            skLineSegment(sketch, "E1069", {"start": v(-89.1, -17.22) * mm, "end": v(-88.83, -17.3) * mm});
            skLineSegment(sketch, "E1070", {"start": v(-88.83, -17.3) * mm, "end": v(-88.63, -17.5) * mm});
            skLineSegment(sketch, "E1071", {"start": v(-88.63, -17.5) * mm, "end": v(-88.6, -17.56) * mm});
            skLineSegment(sketch, "E1072", {"start": v(-88.6, -17.56) * mm, "end": v(-88.55, -17.64) * mm});
            skLineSegment(sketch, "E1073", {"start": v(-88.55, -17.64) * mm, "end": v(-88.08, -18.58) * mm});
            skLineSegment(sketch, "E1074", {"start": v(-88.08, -18.58) * mm, "end": v(-88.02, -18.67) * mm});
            skLineSegment(sketch, "E1075", {"start": v(-88.02, -18.67) * mm, "end": v(-86.93, -18.7) * mm});
            skLineSegment(sketch, "E1076", {"start": v(-86.93, -18.7) * mm, "end": v(-87.02, -18.63) * mm});
            skLineSegment(sketch, "E1077", {"start": v(-87.02, -18.63) * mm, "end": v(-87.33, -18.26) * mm});
            skLineSegment(sketch, "E1078", {"start": v(-87.33, -18.26) * mm, "end": v(-87.55, -17.84) * mm});
            skLineSegment(sketch, "E1079", {"start": v(-87.55, -17.84) * mm, "end": v(-87.6, -17.75) * mm});
            skLineSegment(sketch, "E1080", {"start": v(-88.12, -16.13) * mm, "end": v(-88.12, -16.23) * mm});
            skLineSegment(sketch, "E1081", {"start": v(-88.12, -16.23) * mm, "end": v(-88.33, -16.52) * mm});
            skLineSegment(sketch, "E1082", {"start": v(-88.33, -16.52) * mm, "end": v(-88.75, -16.64) * mm});
            skLineSegment(sketch, "E1083", {"start": v(-88.75, -16.64) * mm, "end": v(-88.9, -16.64) * mm});
            skLineSegment(sketch, "E1084", {"start": v(-88.9, -16.64) * mm, "end": v(-89.75, -16.64) * mm});
            skLineSegment(sketch, "E1085", {"start": v(-89.75, -16.64) * mm, "end": v(-89.75, -15.62) * mm});
            skLineSegment(sketch, "E1086", {"start": v(-89.75, -15.62) * mm, "end": v(-88.9, -15.62) * mm});
            skLineSegment(sketch, "E1087", {"start": v(-88.9, -15.62) * mm, "end": v(-88.75, -15.62) * mm});
            skLineSegment(sketch, "E1088", {"start": v(-88.75, -15.62) * mm, "end": v(-88.33, -15.73) * mm});
            skLineSegment(sketch, "E1089", {"start": v(-88.33, -15.73) * mm, "end": v(-88.12, -16.03) * mm});
            skLineSegment(sketch, "E1090", {"start": v(-88.12, -16.03) * mm, "end": v(-88.12, -16.13) * mm});
            skLineSegment(sketch, "E1091", {"start": v(-85.52, -17.82) * mm, "end": v(-85.57, -17.77) * mm});
            skLineSegment(sketch, "E1092", {"start": v(-85.57, -17.77) * mm, "end": v(-85.76, -17.43) * mm});
            skLineSegment(sketch, "E1093", {"start": v(-85.76, -17.43) * mm, "end": v(-85.84, -17) * mm});
            skLineSegment(sketch, "E1094", {"start": v(-85.84, -17) * mm, "end": v(-85.84, -16.86) * mm});
            skLineSegment(sketch, "E1095", {"start": v(-85.84, -16.86) * mm, "end": v(-85.84, -16.71) * mm});
            skLineSegment(sketch, "E1096", {"start": v(-85.84, -16.71) * mm, "end": v(-85.76, -16.28) * mm});
            skLineSegment(sketch, "E1097", {"start": v(-85.76, -16.28) * mm, "end": v(-85.57, -15.93) * mm});
            skLineSegment(sketch, "E1098", {"start": v(-85.57, -15.93) * mm, "end": v(-85.52, -15.88) * mm});
            skLineSegment(sketch, "E1099", {"start": v(-85.52, -15.88) * mm, "end": v(-85.47, -15.83) * mm});
            skLineSegment(sketch, "E1100", {"start": v(-85.47, -15.83) * mm, "end": v(-84.92, -15.58) * mm});
            skLineSegment(sketch, "E1101", {"start": v(-84.92, -15.58) * mm, "end": v(-84.73, -15.58) * mm});
            skLineSegment(sketch, "E1102", {"start": v(-84.73, -15.58) * mm, "end": v(-84.54, -15.58) * mm});
            skLineSegment(sketch, "E1103", {"start": v(-84.54, -15.58) * mm, "end": v(-84.01, -15.83) * mm});
            skLineSegment(sketch, "E1104", {"start": v(-84.01, -15.83) * mm, "end": v(-83.96, -15.88) * mm});
            skLineSegment(sketch, "E1105", {"start": v(-83.96, -15.88) * mm, "end": v(-83.9, -15.93) * mm});
            skLineSegment(sketch, "E1106", {"start": v(-83.9, -15.93) * mm, "end": v(-83.64, -16.62) * mm});
            skLineSegment(sketch, "E1107", {"start": v(-83.64, -16.62) * mm, "end": v(-83.64, -16.86) * mm});
            skLineSegment(sketch, "E1108", {"start": v(-83.64, -16.86) * mm, "end": v(-83.64, -17.1) * mm});
            skLineSegment(sketch, "E1109", {"start": v(-83.64, -17.1) * mm, "end": v(-83.9, -17.77) * mm});
            skLineSegment(sketch, "E1110", {"start": v(-83.9, -17.77) * mm, "end": v(-83.96, -17.82) * mm});
            skLineSegment(sketch, "E1111", {"start": v(-83.96, -17.82) * mm, "end": v(-84.01, -17.86) * mm});
            skLineSegment(sketch, "E1112", {"start": v(-84.01, -17.86) * mm, "end": v(-84.55, -18.14) * mm});
            skLineSegment(sketch, "E1113", {"start": v(-84.55, -18.14) * mm, "end": v(-84.73, -18.14) * mm});
            skLineSegment(sketch, "E1114", {"start": v(-84.73, -18.14) * mm, "end": v(-84.93, -18.14) * mm});
            skLineSegment(sketch, "E1115", {"start": v(-84.93, -18.14) * mm, "end": v(-85.47, -17.86) * mm});
            skLineSegment(sketch, "E1116", {"start": v(-85.47, -17.86) * mm, "end": v(-85.52, -17.82) * mm});
            skLineSegment(sketch, "E1117", {"start": v(-84.75, -18.78) * mm, "end": v(-84.58, -18.78) * mm});
            skLineSegment(sketch, "E1118", {"start": v(-84.58, -18.78) * mm, "end": v(-84.05, -18.67) * mm});
            skLineSegment(sketch, "E1119", {"start": v(-84.05, -18.67) * mm, "end": v(-83.57, -18.42) * mm});
            skLineSegment(sketch, "E1120", {"start": v(-83.57, -18.42) * mm, "end": v(-83.5, -18.35) * mm});
            skLineSegment(sketch, "E1121", {"start": v(-83.5, -18.35) * mm, "end": v(-83.4, -18.27) * mm});
            skLineSegment(sketch, "E1122", {"start": v(-83.4, -18.27) * mm, "end": v(-83.02, -17.74) * mm});
            skLineSegment(sketch, "E1123", {"start": v(-83.02, -17.74) * mm, "end": v(-82.83, -17.08) * mm});
            skLineSegment(sketch, "E1124", {"start": v(-82.83, -17.08) * mm, "end": v(-82.83, -16.86) * mm});
            skLineSegment(sketch, "E1125", {"start": v(-82.83, -16.86) * mm, "end": v(-82.83, -16.63) * mm});
            skLineSegment(sketch, "E1126", {"start": v(-82.83, -16.63) * mm, "end": v(-83.02, -15.97) * mm});
            skLineSegment(sketch, "E1127", {"start": v(-83.02, -15.97) * mm, "end": v(-83.4, -15.43) * mm});
            skLineSegment(sketch, "E1128", {"start": v(-83.4, -15.43) * mm, "end": v(-83.5, -15.34) * mm});
            skLineSegment(sketch, "E1129", {"start": v(-83.5, -15.34) * mm, "end": v(-83.57, -15.28) * mm});
            skLineSegment(sketch, "E1130", {"start": v(-83.57, -15.28) * mm, "end": v(-84.05, -15.04) * mm});
            skLineSegment(sketch, "E1131", {"start": v(-84.05, -15.04) * mm, "end": v(-84.58, -14.94) * mm});
            skLineSegment(sketch, "E1132", {"start": v(-84.58, -14.94) * mm, "end": v(-84.75, -14.94) * mm});
            skLineSegment(sketch, "E1133", {"start": v(-84.75, -14.94) * mm, "end": v(-84.92, -14.94) * mm});
            skLineSegment(sketch, "E1134", {"start": v(-84.92, -14.94) * mm, "end": v(-85.44, -15.04) * mm});
            skLineSegment(sketch, "E1135", {"start": v(-85.44, -15.04) * mm, "end": v(-85.91, -15.28) * mm});
            skLineSegment(sketch, "E1136", {"start": v(-85.91, -15.28) * mm, "end": v(-86, -15.34) * mm});
            skLineSegment(sketch, "E1137", {"start": v(-86, -15.34) * mm, "end": v(-86.09, -15.43) * mm});
            skLineSegment(sketch, "E1138", {"start": v(-86.09, -15.43) * mm, "end": v(-86.47, -15.97) * mm});
            skLineSegment(sketch, "E1139", {"start": v(-86.47, -15.97) * mm, "end": v(-86.65, -16.63) * mm});
            skLineSegment(sketch, "E1140", {"start": v(-86.65, -16.63) * mm, "end": v(-86.65, -16.86) * mm});
            skLineSegment(sketch, "E1141", {"start": v(-86.65, -16.86) * mm, "end": v(-86.65, -17.08) * mm});
            skLineSegment(sketch, "E1142", {"start": v(-86.65, -17.08) * mm, "end": v(-86.47, -17.74) * mm});
            skLineSegment(sketch, "E1143", {"start": v(-86.47, -17.74) * mm, "end": v(-86.09, -18.27) * mm});
            skLineSegment(sketch, "E1144", {"start": v(-86.09, -18.27) * mm, "end": v(-86, -18.35) * mm});
            skLineSegment(sketch, "E1145", {"start": v(-86, -18.35) * mm, "end": v(-85.91, -18.42) * mm});
            skLineSegment(sketch, "E1146", {"start": v(-85.91, -18.42) * mm, "end": v(-85.44, -18.67) * mm});
            skLineSegment(sketch, "E1147", {"start": v(-85.44, -18.67) * mm, "end": v(-84.92, -18.78) * mm});
            skLineSegment(sketch, "E1148", {"start": v(-84.92, -18.78) * mm, "end": v(-84.75, -18.78) * mm});
            skLineSegment(sketch, "E1149", {"start": v(-79.97, -15.02) * mm, "end": v(-79.95, -15.04) * mm});
            skLineSegment(sketch, "E1150", {"start": v(-79.95, -15.04) * mm, "end": v(-79.86, -15.21) * mm});
            skLineSegment(sketch, "E1151", {"start": v(-79.86, -15.21) * mm, "end": v(-79.87, -15.24) * mm});
            skLineSegment(sketch, "E1152", {"start": v(-79.87, -15.24) * mm, "end": v(-79.97, -15.54) * mm});
            skLineSegment(sketch, "E1153", {"start": v(-79.97, -15.54) * mm, "end": v(-80, -15.58) * mm});
            skLineSegment(sketch, "E1154", {"start": v(-80, -15.58) * mm, "end": v(-80.72, -16.62) * mm});
            skLineSegment(sketch, "E1155", {"start": v(-80.72, -16.62) * mm, "end": v(-81.45, -15.55) * mm});
            skLineSegment(sketch, "E1156", {"start": v(-81.45, -15.55) * mm, "end": v(-81.47, -15.52) * mm});
            skLineSegment(sketch, "E1157", {"start": v(-81.47, -15.52) * mm, "end": v(-81.6, -15.22) * mm});
            skLineSegment(sketch, "E1158", {"start": v(-81.6, -15.22) * mm, "end": v(-81.6, -15.2) * mm});
            skLineSegment(sketch, "E1159", {"start": v(-81.6, -15.2) * mm, "end": v(-81.59, -15.18) * mm});
            skLineSegment(sketch, "E1160", {"start": v(-81.59, -15.18) * mm, "end": v(-81.49, -15.03) * mm});
            skLineSegment(sketch, "E1161", {"start": v(-81.49, -15.03) * mm, "end": v(-81.47, -15.02) * mm});
            skLineSegment(sketch, "E1162", {"start": v(-81.47, -15.02) * mm, "end": v(-82.94, -15.02) * mm});
            skLineSegment(sketch, "E1163", {"start": v(-82.94, -15.02) * mm, "end": v(-82.88, -15.05) * mm});
            skLineSegment(sketch, "E1164", {"start": v(-82.88, -15.05) * mm, "end": v(-82.41, -15.53) * mm});
            skLineSegment(sketch, "E1165", {"start": v(-82.41, -15.53) * mm, "end": v(-82.36, -15.6) * mm});
            skLineSegment(sketch, "E1166", {"start": v(-82.36, -15.6) * mm, "end": v(-81.17, -17.28) * mm});
            skLineSegment(sketch, "E1167", {"start": v(-81.17, -17.28) * mm, "end": v(-81.17, -17.88) * mm});
            skLineSegment(sketch, "E1168", {"start": v(-81.17, -17.88) * mm, "end": v(-81.17, -18) * mm});
            skLineSegment(sketch, "E1169", {"start": v(-81.17, -18) * mm, "end": v(-81.24, -18.35) * mm});
            skLineSegment(sketch, "E1170", {"start": v(-81.24, -18.35) * mm, "end": v(-81.4, -18.64) * mm});
            skLineSegment(sketch, "E1171", {"start": v(-81.4, -18.64) * mm, "end": v(-81.45, -18.67) * mm});
            skLineSegment(sketch, "E1172", {"start": v(-81.45, -18.67) * mm, "end": v(-80.12, -18.67) * mm});
            skLineSegment(sketch, "E1173", {"start": v(-80.12, -18.67) * mm, "end": v(-80.17, -18.64) * mm});
            skLineSegment(sketch, "E1174", {"start": v(-80.17, -18.64) * mm, "end": v(-80.33, -18.35) * mm});
            skLineSegment(sketch, "E1175", {"start": v(-80.33, -18.35) * mm, "end": v(-80.4, -18) * mm});
            skLineSegment(sketch, "E1176", {"start": v(-80.4, -18) * mm, "end": v(-80.4, -17.88) * mm});
            skLineSegment(sketch, "E1177", {"start": v(-80.4, -17.88) * mm, "end": v(-80.4, -17.28) * mm});
            skLineSegment(sketch, "E1178", {"start": v(-80.4, -17.28) * mm, "end": v(-79.31, -15.75) * mm});
            skLineSegment(sketch, "E1179", {"start": v(-79.31, -15.75) * mm, "end": v(-79.27, -15.7) * mm});
            skLineSegment(sketch, "E1180", {"start": v(-79.27, -15.7) * mm, "end": v(-79.01, -15.35) * mm});
            skLineSegment(sketch, "E1181", {"start": v(-79.01, -15.35) * mm, "end": v(-78.71, -15.05) * mm});
            skLineSegment(sketch, "E1182", {"start": v(-78.71, -15.05) * mm, "end": v(-78.65, -15.02) * mm});
            skLineSegment(sketch, "E1183", {"start": v(-78.65, -15.02) * mm, "end": v(-79.97, -15.02) * mm});
            skLineSegment(sketch, "E1184", {"start": v(-72.89, -18.1) * mm, "end": v(-73.83, -18.1) * mm});
            skLineSegment(sketch, "E1185", {"start": v(-73.83, -18.1) * mm, "end": v(-73.83, -17.1) * mm});
            skLineSegment(sketch, "E1186", {"start": v(-73.83, -17.1) * mm, "end": v(-72.42, -17.1) * mm});
            skLineSegment(sketch, "E1187", {"start": v(-72.42, -17.1) * mm, "end": v(-72.33, -16.54) * mm});
            skLineSegment(sketch, "E1188", {"start": v(-72.33, -16.54) * mm, "end": v(-73.83, -16.54) * mm});
            skLineSegment(sketch, "E1189", {"start": v(-73.83, -16.54) * mm, "end": v(-73.83, -15.62) * mm});
            skLineSegment(sketch, "E1190", {"start": v(-73.83, -15.62) * mm, "end": v(-73, -15.62) * mm});
            skLineSegment(sketch, "E1191", {"start": v(-73, -15.62) * mm, "end": v(-72.84, -15.62) * mm});
            skLineSegment(sketch, "E1192", {"start": v(-72.84, -15.62) * mm, "end": v(-72.37, -15.65) * mm});
            skLineSegment(sketch, "E1193", {"start": v(-72.37, -15.65) * mm, "end": v(-72, -15.78) * mm});
            skLineSegment(sketch, "E1194", {"start": v(-72, -15.78) * mm, "end": v(-71.95, -15.83) * mm});
            skLineSegment(sketch, "E1195", {"start": v(-71.95, -15.83) * mm, "end": v(-71.95, -15.02) * mm});
            skLineSegment(sketch, "E1196", {"start": v(-71.95, -15.02) * mm, "end": v(-74.87, -15.02) * mm});
            skLineSegment(sketch, "E1197", {"start": v(-74.87, -15.02) * mm, "end": v(-74.83, -15.05) * mm});
            skLineSegment(sketch, "E1198", {"start": v(-74.83, -15.05) * mm, "end": v(-74.67, -15.36) * mm});
            skLineSegment(sketch, "E1199", {"start": v(-74.67, -15.36) * mm, "end": v(-74.6, -15.71) * mm});
            skLineSegment(sketch, "E1200", {"start": v(-74.6, -15.71) * mm, "end": v(-74.6, -15.83) * mm});
            skLineSegment(sketch, "E1201", {"start": v(-74.6, -15.83) * mm, "end": v(-74.6, -17.88) * mm});
            skLineSegment(sketch, "E1202", {"start": v(-74.6, -17.88) * mm, "end": v(-74.6, -18) * mm});
            skLineSegment(sketch, "E1203", {"start": v(-74.6, -18) * mm, "end": v(-74.67, -18.36) * mm});
            skLineSegment(sketch, "E1204", {"start": v(-74.67, -18.36) * mm, "end": v(-74.83, -18.66) * mm});
            skLineSegment(sketch, "E1205", {"start": v(-74.83, -18.66) * mm, "end": v(-74.87, -18.7) * mm});
            skLineSegment(sketch, "E1206", {"start": v(-74.87, -18.7) * mm, "end": v(-71.93, -18.7) * mm});
            skLineSegment(sketch, "E1207", {"start": v(-71.93, -18.7) * mm, "end": v(-71.8, -17.8) * mm});
            skLineSegment(sketch, "E1208", {"start": v(-71.8, -17.8) * mm, "end": v(-71.85, -17.86) * mm});
            skLineSegment(sketch, "E1209", {"start": v(-71.85, -17.86) * mm, "end": v(-72.25, -18.05) * mm});
            skLineSegment(sketch, "E1210", {"start": v(-72.25, -18.05) * mm, "end": v(-72.73, -18.1) * mm});
            skLineSegment(sketch, "E1211", {"start": v(-72.73, -18.1) * mm, "end": v(-72.89, -18.1) * mm});
            skSolve(sketch);
        }
        {
            var Q0;
            Q0 = qSketchRegion(id + "F0", true);
            extrude(context, id + "F1", {"entities" : qUnion([Q0]), "depth" : 2.54 * mm, "offsetDistance" : 25.4 * mm});
        }
        {
            var Q0;
            Q0=qCreatedBy(makeId("Front.planeOp"),FACE);
            var sketch = newSketch(context, id + "F2", { "sketchPlane" : qUnion([Q0])});
            skLineSegment(sketch, "E1212", {"start": v(-82.8, -8.8) * mm, "end": v(-82.8, -3.05) * mm});
            skLineSegment(sketch, "E1213", {"start": v(-82.8, -3.05) * mm, "end": v(-82.67, -3.05) * mm});
            skLineSegment(sketch, "E1214", {"start": v(-82.67, -3.05) * mm, "end": v(-81.32, -2.98) * mm});
            skLineSegment(sketch, "E1215", {"start": v(-81.32, -2.98) * mm, "end": v(-81.19, -2.96) * mm});
            skLineSegment(sketch, "E1216", {"start": v(-81.19, -2.96) * mm, "end": v(-81.24, -2.85) * mm});
            skLineSegment(sketch, "E1217", {"start": v(-81.24, -2.85) * mm, "end": v(-81.75, -1.75) * mm});
            skLineSegment(sketch, "E1218", {"start": v(-81.75, -1.75) * mm, "end": v(-81.8, -1.64) * mm});
            skLineSegment(sketch, "E1219", {"start": v(-81.8, -1.64) * mm, "end": v(-81.89, -1.65) * mm});
            skLineSegment(sketch, "E1220", {"start": v(-81.89, -1.65) * mm, "end": v(-82.73, -1.7) * mm});
            skLineSegment(sketch, "E1221", {"start": v(-82.73, -1.7) * mm, "end": v(-82.8, -1.7) * mm});
            skLineSegment(sketch, "E1222", {"start": v(-82.8, -1.7) * mm, "end": v(-82.8, -0.51) * mm});
            skLineSegment(sketch, "E1223", {"start": v(-82.8, -0.51) * mm, "end": v(-83, -0.56) * mm});
            skLineSegment(sketch, "E1224", {"start": v(-83, -0.56) * mm, "end": v(-85, -0.87) * mm});
            skLineSegment(sketch, "E1225", {"start": v(-85, -0.87) * mm, "end": v(-85.2, -0.9) * mm});
            skLineSegment(sketch, "E1226", {"start": v(-85.2, -0.9) * mm, "end": v(-85.2, -8.8) * mm});
            skLineSegment(sketch, "E1227", {"start": v(-85.2, -8.8) * mm, "end": v(-85.2, -9.06) * mm});
            skLineSegment(sketch, "E1228", {"start": v(-85.2, -9.06) * mm, "end": v(-85.33, -9.88) * mm});
            skLineSegment(sketch, "E1229", {"start": v(-85.33, -9.88) * mm, "end": v(-85.67, -10.6) * mm});
            skLineSegment(sketch, "E1230", {"start": v(-85.67, -10.6) * mm, "end": v(-86.1, -11.04) * mm});
            skLineSegment(sketch, "E1231", {"start": v(-86.1, -11.04) * mm, "end": v(-86.4, -11.26) * mm});
            skLineSegment(sketch, "E1232", {"start": v(-86.4, -11.26) * mm, "end": v(-86.5, -11.33) * mm});
            skLineSegment(sketch, "E1233", {"start": v(-86.5, -11.33) * mm, "end": v(-81.5, -11.33) * mm});
            skLineSegment(sketch, "E1234", {"start": v(-81.5, -11.33) * mm, "end": v(-81.61, -11.26) * mm});
            skLineSegment(sketch, "E1235", {"start": v(-81.61, -11.26) * mm, "end": v(-81.91, -11.04) * mm});
            skLineSegment(sketch, "E1236", {"start": v(-81.91, -11.04) * mm, "end": v(-82.34, -10.6) * mm});
            skLineSegment(sketch, "E1237", {"start": v(-82.34, -10.6) * mm, "end": v(-82.67, -9.88) * mm});
            skLineSegment(sketch, "E1238", {"start": v(-82.67, -9.88) * mm, "end": v(-82.8, -9.06) * mm});
            skLineSegment(sketch, "E1239", {"start": v(-82.8, -9.06) * mm, "end": v(-82.8, -8.8) * mm});
            skLineSegment(sketch, "E1240", {"start": v(-71.2, -11.3) * mm, "end": v(-71.3, -11.21) * mm});
            skLineSegment(sketch, "E1241", {"start": v(-71.3, -11.21) * mm, "end": v(-71.85, -10.53) * mm});
            skLineSegment(sketch, "E1242", {"start": v(-71.85, -10.53) * mm, "end": v(-72.31, -9.45) * mm});
            skLineSegment(sketch, "E1243", {"start": v(-72.31, -9.45) * mm, "end": v(-72.38, -9.15) * mm});
            skLineSegment(sketch, "E1244", {"start": v(-72.38, -9.15) * mm, "end": v(-72.47, -8.7) * mm});
            skLineSegment(sketch, "E1245", {"start": v(-72.47, -8.7) * mm, "end": v(-72.83, -7.39) * mm});
            skLineSegment(sketch, "E1246", {"start": v(-72.83, -7.39) * mm, "end": v(-73.54, -5.43) * mm});
            skLineSegment(sketch, "E1247", {"start": v(-73.54, -5.43) * mm, "end": v(-74.54, -3.45) * mm});
            skLineSegment(sketch, "E1248", {"start": v(-74.54, -3.45) * mm, "end": v(-75.52, -2.02) * mm});
            skLineSegment(sketch, "E1249", {"start": v(-75.52, -2.02) * mm, "end": v(-75.9, -1.6) * mm});
            skLineSegment(sketch, "E1250", {"start": v(-75.9, -1.6) * mm, "end": v(-75.54, -1.4) * mm});
            skLineSegment(sketch, "E1251", {"start": v(-75.54, -1.4) * mm, "end": v(-74.53, -0.65) * mm});
            skLineSegment(sketch, "E1252", {"start": v(-74.53, -0.65) * mm, "end": v(-73.5, 0.52) * mm});
            skLineSegment(sketch, "E1253", {"start": v(-73.5, 0.52) * mm, "end": v(-72.86, 1.88) * mm});
            skLineSegment(sketch, "E1254", {"start": v(-72.86, 1.88) * mm, "end": v(-72.63, 3.03) * mm});
            skLineSegment(sketch, "E1255", {"start": v(-72.63, 3.03) * mm, "end": v(-72.63, 3.41) * mm});
            skLineSegment(sketch, "E1256", {"start": v(-72.63, 3.41) * mm, "end": v(-72.63, 3.7) * mm});
            skLineSegment(sketch, "E1257", {"start": v(-72.63, 3.7) * mm, "end": v(-72.77, 4.57) * mm});
            skLineSegment(sketch, "E1258", {"start": v(-72.77, 4.57) * mm, "end": v(-73.19, 5.69) * mm});
            skLineSegment(sketch, "E1259", {"start": v(-73.19, 5.69) * mm, "end": v(-73.87, 6.7) * mm});
            skLineSegment(sketch, "E1260", {"start": v(-73.87, 6.7) * mm, "end": v(-74.55, 7.36) * mm});
            skLineSegment(sketch, "E1261", {"start": v(-74.55, 7.36) * mm, "end": v(-74.8, 7.53) * mm});
            skLineSegment(sketch, "E1262", {"start": v(-74.8, 7.53) * mm, "end": v(-74.96, 7.63) * mm});
            skLineSegment(sketch, "E1263", {"start": v(-74.96, 7.63) * mm, "end": v(-75.79, 8.03) * mm});
            skLineSegment(sketch, "E1264", {"start": v(-75.79, 8.03) * mm, "end": v(-76.74, 8.32) * mm});
            skLineSegment(sketch, "E1265", {"start": v(-76.74, 8.32) * mm, "end": v(-76.94, 8.36) * mm});
            skLineSegment(sketch, "E1266", {"start": v(-76.94, 8.36) * mm, "end": v(-76.87, 8.2) * mm});
            skLineSegment(sketch, "E1267", {"start": v(-76.87, 8.2) * mm, "end": v(-76.42, 6.53) * mm});
            skLineSegment(sketch, "E1268", {"start": v(-76.42, 6.53) * mm, "end": v(-76.4, 6.36) * mm});
            skLineSegment(sketch, "E1269", {"start": v(-76.4, 6.36) * mm, "end": v(-76.2, 6.19) * mm});
            skLineSegment(sketch, "E1270", {"start": v(-76.2, 6.19) * mm, "end": v(-75.4, 5.08) * mm});
            skLineSegment(sketch, "E1271", {"start": v(-75.4, 5.08) * mm, "end": v(-75.07, 3.8) * mm});
            skLineSegment(sketch, "E1272", {"start": v(-75.07, 3.8) * mm, "end": v(-75.07, 3.37) * mm});
            skLineSegment(sketch, "E1273", {"start": v(-75.07, 3.37) * mm, "end": v(-75.07, 3.06) * mm});
            skLineSegment(sketch, "E1274", {"start": v(-75.07, 3.06) * mm, "end": v(-75.24, 2.14) * mm});
            skLineSegment(sketch, "E1275", {"start": v(-75.24, 2.14) * mm, "end": v(-75.83, 0.91) * mm});
            skLineSegment(sketch, "E1276", {"start": v(-75.83, 0.91) * mm, "end": v(-76.95, -0.2) * mm});
            skLineSegment(sketch, "E1277", {"start": v(-76.95, -0.2) * mm, "end": v(-78.25, -0.9) * mm});
            skLineSegment(sketch, "E1278", {"start": v(-78.25, -0.9) * mm, "end": v(-78.71, -1.07) * mm});
            skLineSegment(sketch, "E1279", {"start": v(-78.71, -1.07) * mm, "end": v(-78.66, -1.18) * mm});
            skLineSegment(sketch, "E1280", {"start": v(-78.66, -1.18) * mm, "end": v(-78.1, -2.32) * mm});
            skLineSegment(sketch, "E1281", {"start": v(-78.1, -2.32) * mm, "end": v(-78.05, -2.43) * mm});
            skLineSegment(sketch, "E1282", {"start": v(-78.05, -2.43) * mm, "end": v(-78.01, -2.42) * mm});
            skLineSegment(sketch, "E1283", {"start": v(-78.01, -2.42) * mm, "end": v(-77.64, -2.32) * mm});
            skLineSegment(sketch, "E1284", {"start": v(-77.64, -2.32) * mm, "end": v(-77.6, -2.3) * mm});
            skLineSegment(sketch, "E1285", {"start": v(-77.6, -2.3) * mm, "end": v(-77.27, -2.69) * mm});
            skLineSegment(sketch, "E1286", {"start": v(-77.27, -2.69) * mm, "end": v(-75.87, -5.13) * mm});
            skLineSegment(sketch, "E1287", {"start": v(-75.87, -5.13) * mm, "end": v(-74.97, -7.93) * mm});
            skLineSegment(sketch, "E1288", {"start": v(-74.97, -7.93) * mm, "end": v(-74.9, -8.5) * mm});
            skLineSegment(sketch, "E1289", {"start": v(-74.9, -8.5) * mm, "end": v(-74.86, -8.75) * mm});
            skLineSegment(sketch, "E1290", {"start": v(-74.86, -8.75) * mm, "end": v(-74.86, -9.56) * mm});
            skLineSegment(sketch, "E1291", {"start": v(-74.86, -9.56) * mm, "end": v(-75.03, -10.36) * mm});
            skLineSegment(sketch, "E1292", {"start": v(-75.03, -10.36) * mm, "end": v(-75.31, -10.93) * mm});
            skLineSegment(sketch, "E1293", {"start": v(-75.31, -10.93) * mm, "end": v(-75.54, -11.22) * mm});
            skLineSegment(sketch, "E1294", {"start": v(-75.54, -11.22) * mm, "end": v(-75.62, -11.3) * mm});
            skLineSegment(sketch, "E1295", {"start": v(-75.62, -11.3) * mm, "end": v(-71.2, -11.3) * mm});
            skLineSegment(sketch, "E1296", {"start": v(-76.17, -8.73) * mm, "end": v(-76.28, -8.63) * mm});
            skLineSegment(sketch, "E1297", {"start": v(-76.28, -8.63) * mm, "end": v(-76.83, -7.94) * mm});
            skLineSegment(sketch, "E1298", {"start": v(-76.83, -7.94) * mm, "end": v(-77.29, -6.86) * mm});
            skLineSegment(sketch, "E1299", {"start": v(-77.29, -6.86) * mm, "end": v(-77.35, -6.57) * mm});
            skLineSegment(sketch, "E1300", {"start": v(-77.35, -6.57) * mm, "end": v(-77.47, -6.03) * mm});
            skLineSegment(sketch, "E1301", {"start": v(-77.47, -6.03) * mm, "end": v(-78.46, -2.9) * mm});
            skLineSegment(sketch, "E1302", {"start": v(-78.46, -2.9) * mm, "end": v(-80.17, 0.23) * mm});
            skLineSegment(sketch, "E1303", {"start": v(-80.17, 0.23) * mm, "end": v(-80.63, 0.77) * mm});
            skLineSegment(sketch, "E1304", {"start": v(-80.63, 0.77) * mm, "end": v(-80.61, 0.78) * mm});
            skLineSegment(sketch, "E1305", {"start": v(-80.61, 0.78) * mm, "end": v(-80.42, 0.87) * mm});
            skLineSegment(sketch, "E1306", {"start": v(-80.42, 0.87) * mm, "end": v(-80.4, 0.88) * mm});
            skLineSegment(sketch, "E1307", {"start": v(-80.4, 0.88) * mm, "end": v(-80.02, 1.07) * mm});
            skLineSegment(sketch, "E1308", {"start": v(-80.02, 1.07) * mm, "end": v(-78.96, 1.82) * mm});
            skLineSegment(sketch, "E1309", {"start": v(-78.96, 1.82) * mm, "end": v(-77.88, 3.01) * mm});
            skLineSegment(sketch, "E1310", {"start": v(-77.88, 3.01) * mm, "end": v(-77.2, 4.41) * mm});
            skLineSegment(sketch, "E1311", {"start": v(-77.2, 4.41) * mm, "end": v(-76.96, 5.6) * mm});
            skLineSegment(sketch, "E1312", {"start": v(-76.96, 5.6) * mm, "end": v(-76.96, 6) * mm});
            skLineSegment(sketch, "E1313", {"start": v(-76.96, 6) * mm, "end": v(-76.96, 6.29) * mm});
            skLineSegment(sketch, "E1314", {"start": v(-76.96, 6.29) * mm, "end": v(-77.1, 7.16) * mm});
            skLineSegment(sketch, "E1315", {"start": v(-77.1, 7.16) * mm, "end": v(-77.52, 8.28) * mm});
            skLineSegment(sketch, "E1316", {"start": v(-77.52, 8.28) * mm, "end": v(-78.2, 9.29) * mm});
            skLineSegment(sketch, "E1317", {"start": v(-78.2, 9.29) * mm, "end": v(-78.89, 9.94) * mm});
            skLineSegment(sketch, "E1318", {"start": v(-78.89, 9.94) * mm, "end": v(-79.14, 10.11) * mm});
            skLineSegment(sketch, "E1319", {"start": v(-79.14, 10.11) * mm, "end": v(-79.42, 10.3) * mm});
            skLineSegment(sketch, "E1320", {"start": v(-79.42, 10.3) * mm, "end": v(-81.1, 10.92) * mm});
            skLineSegment(sketch, "E1321", {"start": v(-81.1, 10.92) * mm, "end": v(-83, 11.16) * mm});
            skLineSegment(sketch, "E1322", {"start": v(-83, 11.16) * mm, "end": v(-83.64, 11.16) * mm});
            skLineSegment(sketch, "E1323", {"start": v(-83.64, 11.16) * mm, "end": v(-90.83, 11.16) * mm});
            skLineSegment(sketch, "E1324", {"start": v(-90.83, 11.16) * mm, "end": v(-90.73, 11.1) * mm});
            skLineSegment(sketch, "E1325", {"start": v(-90.73, 11.1) * mm, "end": v(-90.42, 10.87) * mm});
            skLineSegment(sketch, "E1326", {"start": v(-90.42, 10.87) * mm, "end": v(-90, 10.43) * mm});
            skLineSegment(sketch, "E1327", {"start": v(-90, 10.43) * mm, "end": v(-89.67, 9.71) * mm});
            skLineSegment(sketch, "E1328", {"start": v(-89.67, 9.71) * mm, "end": v(-89.53, 8.9) * mm});
            skLineSegment(sketch, "E1329", {"start": v(-89.53, 8.9) * mm, "end": v(-89.53, 8.62) * mm});
            skLineSegment(sketch, "E1330", {"start": v(-89.53, 8.62) * mm, "end": v(-89.53, -6.19) * mm});
            skLineSegment(sketch, "E1331", {"start": v(-89.53, -6.19) * mm, "end": v(-89.53, -6.46) * mm});
            skLineSegment(sketch, "E1332", {"start": v(-89.53, -6.46) * mm, "end": v(-89.67, -7.29) * mm});
            skLineSegment(sketch, "E1333", {"start": v(-89.67, -7.29) * mm, "end": v(-90, -8) * mm});
            skLineSegment(sketch, "E1334", {"start": v(-90, -8) * mm, "end": v(-90.42, -8.44) * mm});
            skLineSegment(sketch, "E1335", {"start": v(-90.42, -8.44) * mm, "end": v(-90.73, -8.66) * mm});
            skLineSegment(sketch, "E1336", {"start": v(-90.73, -8.66) * mm, "end": v(-90.83, -8.73) * mm});
            skLineSegment(sketch, "E1337", {"start": v(-90.83, -8.73) * mm, "end": v(-85.84, -8.73) * mm});
            skLineSegment(sketch, "E1338", {"start": v(-85.84, -8.73) * mm, "end": v(-85.94, -8.66) * mm});
            skLineSegment(sketch, "E1339", {"start": v(-85.94, -8.66) * mm, "end": v(-86.24, -8.44) * mm});
            skLineSegment(sketch, "E1340", {"start": v(-86.24, -8.44) * mm, "end": v(-86.67, -8) * mm});
            skLineSegment(sketch, "E1341", {"start": v(-86.67, -8) * mm, "end": v(-87, -7.29) * mm});
            skLineSegment(sketch, "E1342", {"start": v(-87, -7.29) * mm, "end": v(-87.14, -6.46) * mm});
            skLineSegment(sketch, "E1343", {"start": v(-87.14, -6.46) * mm, "end": v(-87.14, -6.19) * mm});
            skLineSegment(sketch, "E1344", {"start": v(-87.14, -6.19) * mm, "end": v(-87.14, -0.45) * mm});
            skLineSegment(sketch, "E1345", {"start": v(-87.14, -0.45) * mm, "end": v(-86.51, -0.45) * mm});
            skLineSegment(sketch, "E1346", {"start": v(-86.51, -0.45) * mm, "end": v(-84.62, -0.3) * mm});
            skLineSegment(sketch, "E1347", {"start": v(-84.62, -0.3) * mm, "end": v(-82.71, 0.04) * mm});
            skLineSegment(sketch, "E1348", {"start": v(-82.71, 0.04) * mm, "end": v(-82.36, 0.13) * mm});
            skLineSegment(sketch, "E1349", {"start": v(-82.36, 0.13) * mm, "end": v(-82.05, -0.25) * mm});
            skLineSegment(sketch, "E1350", {"start": v(-82.05, -0.25) * mm, "end": v(-80.76, -2.64) * mm});
            skLineSegment(sketch, "E1351", {"start": v(-80.76, -2.64) * mm, "end": v(-79.94, -5.35) * mm});
            skLineSegment(sketch, "E1352", {"start": v(-79.94, -5.35) * mm, "end": v(-79.87, -5.89) * mm});
            skLineSegment(sketch, "E1353", {"start": v(-79.87, -5.89) * mm, "end": v(-79.83, -6.15) * mm});
            skLineSegment(sketch, "E1354", {"start": v(-79.83, -6.15) * mm, "end": v(-79.84, -6.96) * mm});
            skLineSegment(sketch, "E1355", {"start": v(-79.84, -6.96) * mm, "end": v(-80, -7.77) * mm});
            skLineSegment(sketch, "E1356", {"start": v(-80, -7.77) * mm, "end": v(-80.29, -8.35) * mm});
            skLineSegment(sketch, "E1357", {"start": v(-80.29, -8.35) * mm, "end": v(-80.5, -8.64) * mm});
            skLineSegment(sketch, "E1358", {"start": v(-80.5, -8.64) * mm, "end": v(-80.6, -8.73) * mm});
            skLineSegment(sketch, "E1359", {"start": v(-80.6, -8.73) * mm, "end": v(-76.17, -8.73) * mm});
            skLineSegment(sketch, "E1360", {"start": v(-87.14, 0.88) * mm, "end": v(-87.14, 9.84) * mm});
            skLineSegment(sketch, "E1361", {"start": v(-87.14, 9.84) * mm, "end": v(-83.75, 9.84) * mm});
            skLineSegment(sketch, "E1362", {"start": v(-83.75, 9.84) * mm, "end": v(-83.44, 9.83) * mm});
            skLineSegment(sketch, "E1363", {"start": v(-83.44, 9.83) * mm, "end": v(-82.12, 9.63) * mm});
            skLineSegment(sketch, "E1364", {"start": v(-82.12, 9.63) * mm, "end": v(-81.05, 9.18) * mm});
            skLineSegment(sketch, "E1365", {"start": v(-81.05, 9.18) * mm, "end": v(-80.87, 9.05) * mm});
            skLineSegment(sketch, "E1366", {"start": v(-80.87, 9.05) * mm, "end": v(-80.63, 8.88) * mm});
            skLineSegment(sketch, "E1367", {"start": v(-80.63, 8.88) * mm, "end": v(-79.77, 7.74) * mm});
            skLineSegment(sketch, "E1368", {"start": v(-79.77, 7.74) * mm, "end": v(-79.4, 6.42) * mm});
            skLineSegment(sketch, "E1369", {"start": v(-79.4, 6.42) * mm, "end": v(-79.4, 5.98) * mm});
            skLineSegment(sketch, "E1370", {"start": v(-79.4, 5.98) * mm, "end": v(-79.4, 5.55) * mm});
            skLineSegment(sketch, "E1371", {"start": v(-79.4, 5.55) * mm, "end": v(-79.73, 4.27) * mm});
            skLineSegment(sketch, "E1372", {"start": v(-79.73, 4.27) * mm, "end": v(-80.93, 2.64) * mm});
            skLineSegment(sketch, "E1373", {"start": v(-80.93, 2.64) * mm, "end": v(-83.3, 1.4) * mm});
            skLineSegment(sketch, "E1374", {"start": v(-83.3, 1.4) * mm, "end": v(-86.18, 0.9) * mm});
            skLineSegment(sketch, "E1375", {"start": v(-86.18, 0.9) * mm, "end": v(-87.14, 0.88) * mm});
            skLineSegment(sketch, "E1376", {"start": v(-82.8, 2.16) * mm, "end": v(-82.8, 7.21) * mm});
            skLineSegment(sketch, "E1377", {"start": v(-82.8, 7.21) * mm, "end": v(-80.12, 7.21) * mm});
            skLineSegment(sketch, "E1378", {"start": v(-80.12, 7.21) * mm, "end": v(-80.17, 7.35) * mm});
            skLineSegment(sketch, "E1379", {"start": v(-80.17, 7.35) * mm, "end": v(-80.52, 7.97) * mm});
            skLineSegment(sketch, "E1380", {"start": v(-80.52, 7.97) * mm, "end": v(-81, 8.47) * mm});
            skLineSegment(sketch, "E1381", {"start": v(-81, 8.47) * mm, "end": v(-81.12, 8.56) * mm});
            skLineSegment(sketch, "E1382", {"start": v(-81.12, 8.56) * mm, "end": v(-86.5, 8.56) * mm});
            skLineSegment(sketch, "E1383", {"start": v(-86.5, 8.56) * mm, "end": v(-86.4, 8.5) * mm});
            skLineSegment(sketch, "E1384", {"start": v(-86.4, 8.5) * mm, "end": v(-86.1, 8.28) * mm});
            skLineSegment(sketch, "E1385", {"start": v(-86.1, 8.28) * mm, "end": v(-85.67, 7.83) * mm});
            skLineSegment(sketch, "E1386", {"start": v(-85.67, 7.83) * mm, "end": v(-85.33, 7.12) * mm});
            skLineSegment(sketch, "E1387", {"start": v(-85.33, 7.12) * mm, "end": v(-85.2, 6.3) * mm});
            skLineSegment(sketch, "E1388", {"start": v(-85.2, 6.3) * mm, "end": v(-85.2, 6.02) * mm});
            skLineSegment(sketch, "E1389", {"start": v(-85.2, 6.02) * mm, "end": v(-85.2, 1.56) * mm});
            skLineSegment(sketch, "E1390", {"start": v(-85.2, 1.56) * mm, "end": v(-84.98, 1.6) * mm});
            skLineSegment(sketch, "E1391", {"start": v(-84.98, 1.6) * mm, "end": v(-82.98, 2.09) * mm});
            skLineSegment(sketch, "E1392", {"start": v(-82.98, 2.09) * mm, "end": v(-82.8, 2.16) * mm});
            skSolve(sketch);
        }
        {
            var Q0;
            Q0 = qSketchRegion(id + "F2", true);
            extrude(context, id + "F3", {"entities" : qUnion([Q0]), "depth" : 2.54 * mm, "offsetDistance" : 25.4 * mm});
        }
        {
            var Q0;
            Q0=qCreatedBy(makeId("Front.planeOp"),FACE);
            var sketch = newSketch(context, id + "F4", { "sketchPlane" : qUnion([Q0])});
            skLineSegment(sketch, "E1393", {"start": v(-82.8, 2.16) * mm, "end": v(-82.8, 7.21) * mm});
            skLineSegment(sketch, "E1394", {"start": v(-82.8, 7.21) * mm, "end": v(-80.12, 7.21) * mm});
            skLineSegment(sketch, "E1395", {"start": v(-80.12, 7.21) * mm, "end": v(-80.17, 7.35) * mm});
            skLineSegment(sketch, "E1396", {"start": v(-80.17, 7.35) * mm, "end": v(-80.52, 7.97) * mm});
            skLineSegment(sketch, "E1397", {"start": v(-80.52, 7.97) * mm, "end": v(-81, 8.47) * mm});
            skLineSegment(sketch, "E1398", {"start": v(-81, 8.47) * mm, "end": v(-81.12, 8.56) * mm});
            skLineSegment(sketch, "E1399", {"start": v(-81.12, 8.56) * mm, "end": v(-86.5, 8.56) * mm});
            skLineSegment(sketch, "E1400", {"start": v(-86.5, 8.56) * mm, "end": v(-86.4, 8.5) * mm});
            skLineSegment(sketch, "E1401", {"start": v(-86.4, 8.5) * mm, "end": v(-86.1, 8.28) * mm});
            skLineSegment(sketch, "E1402", {"start": v(-86.1, 8.28) * mm, "end": v(-85.67, 7.83) * mm});
            skLineSegment(sketch, "E1403", {"start": v(-85.67, 7.83) * mm, "end": v(-85.33, 7.12) * mm});
            skLineSegment(sketch, "E1404", {"start": v(-85.33, 7.12) * mm, "end": v(-85.2, 6.3) * mm});
            skLineSegment(sketch, "E1405", {"start": v(-85.2, 6.3) * mm, "end": v(-85.2, 6.02) * mm});
            skLineSegment(sketch, "E1406", {"start": v(-85.2, 6.02) * mm, "end": v(-85.2, 1.56) * mm});
            skLineSegment(sketch, "E1407", {"start": v(-85.2, 1.56) * mm, "end": v(-84.98, 1.6) * mm});
            skLineSegment(sketch, "E1408", {"start": v(-84.98, 1.6) * mm, "end": v(-82.98, 2.09) * mm});
            skLineSegment(sketch, "E1409", {"start": v(-82.98, 2.09) * mm, "end": v(-82.8, 2.16) * mm});
            skSolve(sketch);
        }
        {
            var Q0;
            Q0 = qSketchRegion(id + "F4", true);
            extrude(context, id + "F5", {"entities" : qUnion([Q0]), "operationType" : NewBodyOperationType.REMOVE, "oppositeDirection" : true, "depth" : 0.76 * mm, "offsetDistance" : 25.4 * mm});
        }
        {
            var Q0;
            Q0=qCreatedBy(makeId("Front.planeOp"),FACE);
            var sketch = newSketch(context, id + "F6", { "sketchPlane" : qUnion([Q0])});
            skLineSegment(sketch, "E1410", {"start": v(-67.7, 18.27) * mm, "end": v(-67.7, 18.64) * mm});
            skLineSegment(sketch, "E1411", {"start": v(-67.7, 18.64) * mm, "end": v(-68, 19.75) * mm});
            skLineSegment(sketch, "E1412", {"start": v(-68, 19.75) * mm, "end": v(-68.82, 20.97) * mm});
            skLineSegment(sketch, "E1413", {"start": v(-68.82, 20.97) * mm, "end": v(-70.04, 21.79) * mm});
            skLineSegment(sketch, "E1414", {"start": v(-70.04, 21.79) * mm, "end": v(-71.15, 22.08) * mm});
            skLineSegment(sketch, "E1415", {"start": v(-71.15, 22.08) * mm, "end": v(-71.52, 22.08) * mm});
            skLineSegment(sketch, "E1416", {"start": v(-71.52, 22.08) * mm, "end": v(-90.92, 22.08) * mm});
            skLineSegment(sketch, "E1417", {"start": v(-90.92, 22.08) * mm, "end": v(-91.3, 22.08) * mm});
            skLineSegment(sketch, "E1418", {"start": v(-91.3, 22.08) * mm, "end": v(-92.4, 21.79) * mm});
            skLineSegment(sketch, "E1419", {"start": v(-92.4, 21.79) * mm, "end": v(-93.62, 20.97) * mm});
            skLineSegment(sketch, "E1420", {"start": v(-93.62, 20.97) * mm, "end": v(-94.44, 19.75) * mm});
            skLineSegment(sketch, "E1421", {"start": v(-94.44, 19.75) * mm, "end": v(-94.74, 18.64) * mm});
            skLineSegment(sketch, "E1422", {"start": v(-94.74, 18.64) * mm, "end": v(-94.74, 18.27) * mm});
            skLineSegment(sketch, "E1423", {"start": v(-94.74, 18.27) * mm, "end": v(-94.74, -18.26) * mm});
            skLineSegment(sketch, "E1424", {"start": v(-94.74, -18.26) * mm, "end": v(-94.74, -18.64) * mm});
            skLineSegment(sketch, "E1425", {"start": v(-94.74, -18.64) * mm, "end": v(-94.44, -19.75) * mm});
            skLineSegment(sketch, "E1426", {"start": v(-94.44, -19.75) * mm, "end": v(-93.62, -20.97) * mm});
            skLineSegment(sketch, "E1427", {"start": v(-93.62, -20.97) * mm, "end": v(-92.4, -21.78) * mm});
            skLineSegment(sketch, "E1428", {"start": v(-92.4, -21.78) * mm, "end": v(-91.3, -22.08) * mm});
            skLineSegment(sketch, "E1429", {"start": v(-91.3, -22.08) * mm, "end": v(-90.92, -22.08) * mm});
            skLineSegment(sketch, "E1430", {"start": v(-90.92, -22.08) * mm, "end": v(-71.52, -22.08) * mm});
            skLineSegment(sketch, "E1431", {"start": v(-71.52, -22.08) * mm, "end": v(-71.15, -22.08) * mm});
            skLineSegment(sketch, "E1432", {"start": v(-71.15, -22.08) * mm, "end": v(-70.04, -21.78) * mm});
            skLineSegment(sketch, "E1433", {"start": v(-70.04, -21.78) * mm, "end": v(-68.82, -20.97) * mm});
            skLineSegment(sketch, "E1434", {"start": v(-68.82, -20.97) * mm, "end": v(-68, -19.75) * mm});
            skLineSegment(sketch, "E1435", {"start": v(-68, -19.75) * mm, "end": v(-67.7, -18.64) * mm});
            skLineSegment(sketch, "E1436", {"start": v(-67.7, -18.64) * mm, "end": v(-67.7, -18.26) * mm});
            skLineSegment(sketch, "E1437", {"start": v(-67.7, -18.26) * mm, "end": v(-67.7, 18.27) * mm});
            skSolve(sketch);
        }
        {
            var Q0;
            Q0 = qSketchRegion(id + "F6", true);
            extrude(context, id + "F7", {"entities" : qUnion([Q0]), "oppositeDirection" : true, "depth" : 2.54 * mm, "offsetDistance" : 25.4 * mm});
        }
    });
